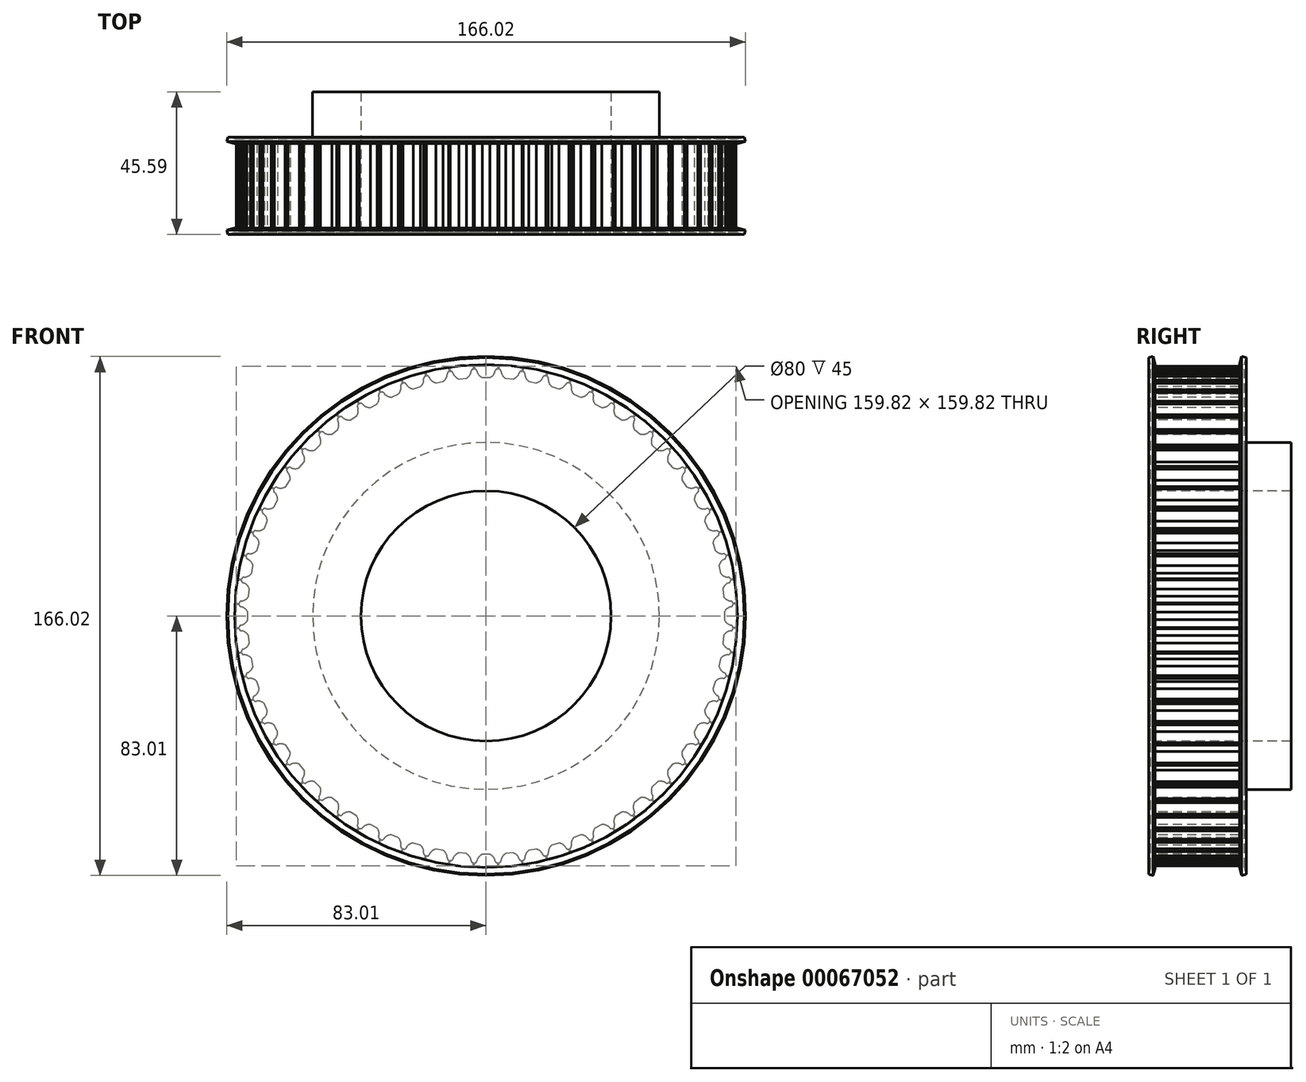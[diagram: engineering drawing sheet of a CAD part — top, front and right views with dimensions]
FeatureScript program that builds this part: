
annotation { "Feature Type Name" : "Feature", "Feature Type Description" : "" }
export const myFeature = defineFeature(function(context is Context, id is Id, definition is map)
    precondition{}
    {
        {
            var Q0;
            Q0=qCreatedBy(makeId("Right.planeOp"),FACE);
            var sketch = newSketch(context, id + "F0", { "sketchPlane" : qUnion([Q0])});
            skLineSegment(sketch, "E0", {"start": v(-21.52, 0) * mm, "end": v(23.89, 0) * mm, "construction": true});
            skLineSegment(sketch, "E1", {"start": v(0, 40) * mm, "end": v(0, 80) * mm});
            skLineSegment(sketch, "E2", {"start": v(0, 80) * mm, "end": v(30, 80) * mm});
            skLineSegment(sketch, "E3", {"start": v(30, 80) * mm, "end": v(30, 55.5) * mm});
            skLineSegment(sketch, "E4", {"start": v(30, 55.5) * mm, "end": v(45, 55.5) * mm});
            skLineSegment(sketch, "E5", {"start": v(45, 55.5) * mm, "end": v(45, 40) * mm});
            skLineSegment(sketch, "E6", {"start": v(45, 40) * mm, "end": v(0, 40) * mm});
            skSolve(sketch);
        }
        {
            var Q0;
            Q0=qSketchRegion(id+"F0",true);
            var Q1;
            Q1=sQuery(id+"F0.wireOp",EDGE,"E0");
            revolve(context, id + "F1", {"entities" : qUnion([Q0]), "axis" : qUnion([Q1]), "revolveType" : RevolveType.FULL});
        }
        {
            var Q0;
            Q0=qCreatedBy(makeId("Right.planeOp"),FACE);
            var sketch = newSketch(context, id + "F2", { "sketchPlane" : qUnion([Q0])});
            skLineSegment(sketch, "E7", {"start": v(-38.96, 0) * mm, "end": v(60.95, 0) * mm, "construction": true});
            skSolve(sketch);
        }
        {
            var Q0;
            Q0=makeQuery(id+"F1.opRevolve","SWEPT_FACE",FACE,{"disambiguationData":[OSD([sQuery(id+"F0.wireOp",EDGE,"E1")])]});
            var sketch = newSketch(context, id + "F3", { "sketchPlane" : qUnion([Q0])});
            skLineSegment(sketch, "E8.bottom", {"start": v(-3.75, 81) * mm, "end": v(3.75, 81) * mm});
            skLineSegment(sketch, "E8.top", {"start": v(3.67, 79) * mm, "end": v(3.75, 79) * mm});
            skLineSegment(sketch, "E8.left", {"start": v(-3.75, 81) * mm, "end": v(-3.75, 79) * mm});
            skLineSegment(sketch, "E8.right", {"start": v(3.75, 81) * mm, "end": v(3.75, 79) * mm});
            skArc(sketch, "E9", {"start": v(-2.94, 78.4) * mm, "mid": v(-2.33, 77.11) * mm, "end": v(-1.2, 76.25) * mm});
            skLineSegment(sketch, "E10", {"start": v(-1.2, 76.25) * mm, "end": v(1.2, 76.25) * mm});
            skArc(sketch, "E11.trimOffspring", {"start": v(1.2, 76.25) * mm, "mid": v(2.33, 77.11) * mm, "end": v(2.94, 78.4) * mm});
            skArc(sketch, "E12.filletArc", {"start": v(3.67, 79) * mm, "mid": v(3.2, 78.83) * mm, "end": v(2.94, 78.4) * mm});
            skLineSegment(sketch, "E13", {"start": v(-3.75, 79) * mm, "end": v(-3.67, 79) * mm});
            skPoint(sketch, "E14.visualSharp", {"position": v(-3, 79) * mm});
            skArc(sketch, "E14.filletArc", {"start": v(-2.94, 78.4) * mm, "mid": v(-3.2, 78.83) * mm, "end": v(-3.67, 79) * mm});
            skLineSegment(sketch, "E15.1.0", {"start": v(-11.67, 80.24) * mm, "end": v(-4.2, 80.98) * mm});
            skLineSegment(sketch, "E15.1.1", {"start": v(-11.67, 80.24) * mm, "end": v(-11.48, 78.25) * mm});
            skLineSegment(sketch, "E15.1.2", {"start": v(-11.48, 78.25) * mm, "end": v(-11.4, 78.26) * mm});
            skArc(sketch, "E15.1.3", {"start": v(-10.6, 77.73) * mm, "mid": v(-10.91, 78.14) * mm, "end": v(-11.4, 78.26) * mm});
            skArc(sketch, "E15.1.4", {"start": v(-10.6, 77.73) * mm, "mid": v(-9.88, 76.51) * mm, "end": v(-8.67, 75.77) * mm});
            skLineSegment(sketch, "E15.1.5", {"start": v(-8.67, 75.77) * mm, "end": v(-6.28, 76) * mm});
            skArc(sketch, "E15.1.6", {"start": v(-6.28, 76) * mm, "mid": v(-5.24, 76.97) * mm, "end": v(-4.76, 78.31) * mm});
            skArc(sketch, "E15.1.7", {"start": v(-4.09, 78.98) * mm, "mid": v(-4.54, 78.76) * mm, "end": v(-4.76, 78.31) * mm});
            skLineSegment(sketch, "E15.1.8", {"start": v(-4.09, 78.98) * mm, "end": v(-4.01, 78.99) * mm});
            skLineSegment(sketch, "E15.1.9", {"start": v(-4.2, 80.98) * mm, "end": v(-4.01, 78.99) * mm});
            skLineSegment(sketch, "E15.2.0", {"start": v(-19.48, 78.71) * mm, "end": v(-12.12, 80.18) * mm});
            skLineSegment(sketch, "E15.2.1", {"start": v(-19.48, 78.71) * mm, "end": v(-19.1, 76.75) * mm});
            skLineSegment(sketch, "E15.2.2", {"start": v(-19.1, 76.75) * mm, "end": v(-19.02, 76.77) * mm});
            skArc(sketch, "E15.2.3", {"start": v(-18.18, 76.32) * mm, "mid": v(-18.52, 76.7) * mm, "end": v(-19.02, 76.77) * mm});
            skArc(sketch, "E15.2.4", {"start": v(-18.18, 76.32) * mm, "mid": v(-17.33, 75.18) * mm, "end": v(-16.05, 74.55) * mm});
            skLineSegment(sketch, "E15.2.5", {"start": v(-16.05, 74.55) * mm, "end": v(-13.7, 75.02) * mm});
            skArc(sketch, "E15.2.6", {"start": v(-13.7, 75.02) * mm, "mid": v(-12.76, 76.09) * mm, "end": v(-12.41, 77.47) * mm});
            skArc(sketch, "E15.2.7", {"start": v(-11.8, 78.2) * mm, "mid": v(-12.24, 77.94) * mm, "end": v(-12.41, 77.47) * mm});
            skLineSegment(sketch, "E15.2.8", {"start": v(-11.8, 78.2) * mm, "end": v(-11.73, 78.21) * mm});
            skLineSegment(sketch, "E15.2.9", {"start": v(-12.12, 80.18) * mm, "end": v(-11.73, 78.21) * mm});
            skLineSegment(sketch, "E15.3.0", {"start": v(-27.1, 76.42) * mm, "end": v(-19.92, 78.6) * mm});
            skLineSegment(sketch, "E15.3.1", {"start": v(-27.1, 76.42) * mm, "end": v(-26.52, 74.5) * mm});
            skLineSegment(sketch, "E15.3.2", {"start": v(-26.52, 74.5) * mm, "end": v(-26.45, 74.53) * mm});
            skArc(sketch, "E15.3.3", {"start": v(-25.57, 74.17) * mm, "mid": v(-25.95, 74.5) * mm, "end": v(-26.45, 74.53) * mm});
            skArc(sketch, "E15.3.4", {"start": v(-25.57, 74.17) * mm, "mid": v(-24.62, 73.12) * mm, "end": v(-23.28, 72.62) * mm});
            skLineSegment(sketch, "E15.3.5", {"start": v(-23.28, 72.62) * mm, "end": v(-20.99, 73.31) * mm});
            skArc(sketch, "E15.3.6", {"start": v(-20.99, 73.31) * mm, "mid": v(-20.15, 74.47) * mm, "end": v(-19.95, 75.88) * mm});
            skArc(sketch, "E15.3.7", {"start": v(-19.42, 76.66) * mm, "mid": v(-19.82, 76.37) * mm, "end": v(-19.95, 75.88) * mm});
            skLineSegment(sketch, "E15.3.8", {"start": v(-19.42, 76.66) * mm, "end": v(-19.34, 76.69) * mm});
            skLineSegment(sketch, "E15.3.9", {"start": v(-19.92, 78.6) * mm, "end": v(-19.34, 76.69) * mm});
            skLineSegment(sketch, "E15.4.0", {"start": v(-34.46, 73.4) * mm, "end": v(-27.53, 76.27) * mm});
            skLineSegment(sketch, "E15.4.1", {"start": v(-34.46, 73.4) * mm, "end": v(-33.7, 71.55) * mm});
            skLineSegment(sketch, "E15.4.2", {"start": v(-33.7, 71.55) * mm, "end": v(-33.63, 71.58) * mm});
            skArc(sketch, "E15.4.3", {"start": v(-32.72, 71.3) * mm, "mid": v(-33.12, 71.6) * mm, "end": v(-33.63, 71.58) * mm});
            skArc(sketch, "E15.4.4", {"start": v(-32.72, 71.3) * mm, "mid": v(-31.66, 70.35) * mm, "end": v(-30.29, 69.99) * mm});
            skLineSegment(sketch, "E15.4.5", {"start": v(-30.29, 69.99) * mm, "end": v(-28.07, 70.9) * mm});
            skArc(sketch, "E15.4.6", {"start": v(-28.07, 70.9) * mm, "mid": v(-27.36, 72.13) * mm, "end": v(-27.29, 73.56) * mm});
            skArc(sketch, "E15.4.7", {"start": v(-26.84, 74.4) * mm, "mid": v(-27.21, 74.05) * mm, "end": v(-27.29, 73.56) * mm});
            skLineSegment(sketch, "E15.4.8", {"start": v(-26.84, 74.4) * mm, "end": v(-26.77, 74.42) * mm});
            skLineSegment(sketch, "E15.4.9", {"start": v(-27.53, 76.27) * mm, "end": v(-26.77, 74.42) * mm});
            skLineSegment(sketch, "E15.5.0", {"start": v(-41.5, 69.67) * mm, "end": v(-34.88, 73.2) * mm});
            skLineSegment(sketch, "E15.5.1", {"start": v(-41.5, 69.67) * mm, "end": v(-40.55, 67.9) * mm});
            skLineSegment(sketch, "E15.5.2", {"start": v(-40.55, 67.9) * mm, "end": v(-40.48, 67.94) * mm});
            skArc(sketch, "E15.5.3", {"start": v(-39.55, 67.76) * mm, "mid": v(-39.98, 68.01) * mm, "end": v(-40.48, 67.94) * mm});
            skArc(sketch, "E15.5.4", {"start": v(-39.55, 67.76) * mm, "mid": v(-38.4, 66.9) * mm, "end": v(-37, 66.68) * mm});
            skLineSegment(sketch, "E15.5.5", {"start": v(-37, 66.68) * mm, "end": v(-34.89, 67.81) * mm});
            skArc(sketch, "E15.5.6", {"start": v(-34.89, 67.81) * mm, "mid": v(-34.3, 69.1) * mm, "end": v(-34.37, 70.53) * mm});
            skArc(sketch, "E15.5.7", {"start": v(-34, 71.4) * mm, "mid": v(-34.34, 71.03) * mm, "end": v(-34.37, 70.53) * mm});
            skLineSegment(sketch, "E15.5.8", {"start": v(-34, 71.4) * mm, "end": v(-33.93, 71.44) * mm});
            skLineSegment(sketch, "E15.5.9", {"start": v(-34.88, 73.2) * mm, "end": v(-33.93, 71.44) * mm});
            skLineSegment(sketch, "E15.6.0", {"start": v(-48.12, 65.27) * mm, "end": v(-41.88, 69.43) * mm});
            skLineSegment(sketch, "E15.6.1", {"start": v(-48.12, 65.27) * mm, "end": v(-47, 63.6) * mm});
            skLineSegment(sketch, "E15.6.2", {"start": v(-47, 63.6) * mm, "end": v(-46.95, 63.64) * mm});
            skArc(sketch, "E15.6.3", {"start": v(-46, 63.55) * mm, "mid": v(-46.46, 63.77) * mm, "end": v(-46.95, 63.64) * mm});
            skArc(sketch, "E15.6.4", {"start": v(-46, 63.55) * mm, "mid": v(-44.78, 62.82) * mm, "end": v(-43.36, 62.73) * mm});
            skLineSegment(sketch, "E15.6.5", {"start": v(-43.36, 62.73) * mm, "end": v(-41.37, 64.07) * mm});
            skArc(sketch, "E15.6.6", {"start": v(-41.37, 64.07) * mm, "mid": v(-40.9, 65.41) * mm, "end": v(-41.11, 66.82) * mm});
            skArc(sketch, "E15.6.7", {"start": v(-40.84, 67.73) * mm, "mid": v(-41.14, 67.32) * mm, "end": v(-41.11, 66.82) * mm});
            skLineSegment(sketch, "E15.6.8", {"start": v(-40.84, 67.73) * mm, "end": v(-40.77, 67.77) * mm});
            skLineSegment(sketch, "E15.6.9", {"start": v(-41.88, 69.43) * mm, "end": v(-40.77, 67.77) * mm});
            skLineSegment(sketch, "E15.7.0", {"start": v(-54.28, 60.23) * mm, "end": v(-48.49, 65) * mm});
            skLineSegment(sketch, "E15.7.1", {"start": v(-54.28, 60.23) * mm, "end": v(-53.02, 58.69) * mm});
            skLineSegment(sketch, "E15.7.2", {"start": v(-53.02, 58.69) * mm, "end": v(-52.96, 58.74) * mm});
            skArc(sketch, "E15.7.3", {"start": v(-52, 58.74) * mm, "mid": v(-52.48, 58.9) * mm, "end": v(-52.96, 58.74) * mm});
            skArc(sketch, "E15.7.4", {"start": v(-52, 58.74) * mm, "mid": v(-50.72, 58.13) * mm, "end": v(-49.3, 58.18) * mm});
            skLineSegment(sketch, "E15.7.5", {"start": v(-49.3, 58.18) * mm, "end": v(-47.45, 59.7) * mm});
            skArc(sketch, "E15.7.6", {"start": v(-47.45, 59.7) * mm, "mid": v(-47.12, 61.09) * mm, "end": v(-47.46, 62.47) * mm});
            skArc(sketch, "E15.7.7", {"start": v(-47.28, 63.4) * mm, "mid": v(-47.54, 62.97) * mm, "end": v(-47.46, 62.47) * mm});
            skLineSegment(sketch, "E15.7.8", {"start": v(-47.28, 63.4) * mm, "end": v(-47.22, 63.45) * mm});
            skLineSegment(sketch, "E15.7.9", {"start": v(-48.49, 65) * mm, "end": v(-47.22, 63.45) * mm});
            skLineSegment(sketch, "E15.8.0", {"start": v(-59.93, 54.62) * mm, "end": v(-54.62, 59.93) * mm});
            skLineSegment(sketch, "E15.8.1", {"start": v(-59.93, 54.62) * mm, "end": v(-58.51, 53.2) * mm});
            skLineSegment(sketch, "E15.8.2", {"start": v(-58.51, 53.2) * mm, "end": v(-58.46, 53.26) * mm});
            skArc(sketch, "E15.8.3", {"start": v(-57.52, 53.36) * mm, "mid": v(-58, 53.48) * mm, "end": v(-58.46, 53.26) * mm});
            skArc(sketch, "E15.8.4", {"start": v(-57.52, 53.36) * mm, "mid": v(-56.18, 52.88) * mm, "end": v(-54.76, 53.07) * mm});
            skLineSegment(sketch, "E15.8.5", {"start": v(-54.76, 53.07) * mm, "end": v(-53.07, 54.76) * mm});
            skArc(sketch, "E15.8.6", {"start": v(-53.07, 54.76) * mm, "mid": v(-52.88, 56.18) * mm, "end": v(-53.36, 57.52) * mm});
            skArc(sketch, "E15.8.7", {"start": v(-53.26, 58.46) * mm, "mid": v(-53.48, 58) * mm, "end": v(-53.36, 57.52) * mm});
            skLineSegment(sketch, "E15.8.8", {"start": v(-53.26, 58.46) * mm, "end": v(-53.2, 58.51) * mm});
            skLineSegment(sketch, "E15.8.9", {"start": v(-54.62, 59.93) * mm, "end": v(-53.2, 58.51) * mm});
            skLineSegment(sketch, "E15.9.0", {"start": v(-65, 48.49) * mm, "end": v(-60.23, 54.28) * mm});
            skLineSegment(sketch, "E15.9.1", {"start": v(-65, 48.49) * mm, "end": v(-63.45, 47.22) * mm});
            skLineSegment(sketch, "E15.9.2", {"start": v(-63.45, 47.22) * mm, "end": v(-63.4, 47.28) * mm});
            skArc(sketch, "E15.9.3", {"start": v(-62.47, 47.46) * mm, "mid": v(-62.97, 47.54) * mm, "end": v(-63.4, 47.28) * mm});
            skArc(sketch, "E15.9.4", {"start": v(-62.47, 47.46) * mm, "mid": v(-61.09, 47.12) * mm, "end": v(-59.7, 47.45) * mm});
            skLineSegment(sketch, "E15.9.5", {"start": v(-59.7, 47.45) * mm, "end": v(-58.18, 49.3) * mm});
            skArc(sketch, "E15.9.6", {"start": v(-58.18, 49.3) * mm, "mid": v(-58.13, 50.72) * mm, "end": v(-58.74, 52) * mm});
            skArc(sketch, "E15.9.7", {"start": v(-58.74, 52.96) * mm, "mid": v(-58.9, 52.48) * mm, "end": v(-58.74, 52) * mm});
            skLineSegment(sketch, "E15.9.8", {"start": v(-58.74, 52.96) * mm, "end": v(-58.69, 53.02) * mm});
            skLineSegment(sketch, "E15.9.9", {"start": v(-60.23, 54.28) * mm, "end": v(-58.69, 53.02) * mm});
            skLineSegment(sketch, "E15.10.0", {"start": v(-69.43, 41.88) * mm, "end": v(-65.27, 48.12) * mm});
            skLineSegment(sketch, "E15.10.1", {"start": v(-69.43, 41.88) * mm, "end": v(-67.77, 40.77) * mm});
            skLineSegment(sketch, "E15.10.2", {"start": v(-67.77, 40.77) * mm, "end": v(-67.73, 40.84) * mm});
            skArc(sketch, "E15.10.3", {"start": v(-66.82, 41.11) * mm, "mid": v(-67.32, 41.14) * mm, "end": v(-67.73, 40.84) * mm});
            skArc(sketch, "E15.10.4", {"start": v(-66.82, 41.11) * mm, "mid": v(-65.41, 40.9) * mm, "end": v(-64.07, 41.37) * mm});
            skLineSegment(sketch, "E15.10.5", {"start": v(-64.07, 41.37) * mm, "end": v(-62.73, 43.36) * mm});
            skArc(sketch, "E15.10.6", {"start": v(-62.73, 43.36) * mm, "mid": v(-62.82, 44.78) * mm, "end": v(-63.55, 46) * mm});
            skArc(sketch, "E15.10.7", {"start": v(-63.64, 46.95) * mm, "mid": v(-63.77, 46.46) * mm, "end": v(-63.55, 46) * mm});
            skLineSegment(sketch, "E15.10.8", {"start": v(-63.64, 46.95) * mm, "end": v(-63.6, 47) * mm});
            skLineSegment(sketch, "E15.10.9", {"start": v(-65.27, 48.12) * mm, "end": v(-63.6, 47) * mm});
            skLineSegment(sketch, "E15.11.0", {"start": v(-73.2, 34.88) * mm, "end": v(-69.67, 41.5) * mm});
            skLineSegment(sketch, "E15.11.1", {"start": v(-73.2, 34.88) * mm, "end": v(-71.44, 33.93) * mm});
            skLineSegment(sketch, "E15.11.2", {"start": v(-71.44, 33.93) * mm, "end": v(-71.4, 34) * mm});
            skArc(sketch, "E15.11.3", {"start": v(-70.53, 34.37) * mm, "mid": v(-71.03, 34.34) * mm, "end": v(-71.4, 34) * mm});
            skArc(sketch, "E15.11.4", {"start": v(-70.53, 34.37) * mm, "mid": v(-69.1, 34.3) * mm, "end": v(-67.81, 34.89) * mm});
            skLineSegment(sketch, "E15.11.5", {"start": v(-67.81, 34.89) * mm, "end": v(-66.68, 37) * mm});
            skArc(sketch, "E15.11.6", {"start": v(-66.68, 37) * mm, "mid": v(-66.9, 38.4) * mm, "end": v(-67.76, 39.55) * mm});
            skArc(sketch, "E15.11.7", {"start": v(-67.94, 40.48) * mm, "mid": v(-68.01, 39.98) * mm, "end": v(-67.76, 39.55) * mm});
            skLineSegment(sketch, "E15.11.8", {"start": v(-67.94, 40.48) * mm, "end": v(-67.9, 40.55) * mm});
            skLineSegment(sketch, "E15.11.9", {"start": v(-69.67, 41.5) * mm, "end": v(-67.9, 40.55) * mm});
            skLineSegment(sketch, "E15.12.0", {"start": v(-76.27, 27.53) * mm, "end": v(-73.4, 34.46) * mm});
            skLineSegment(sketch, "E15.12.1", {"start": v(-76.27, 27.53) * mm, "end": v(-74.42, 26.77) * mm});
            skLineSegment(sketch, "E15.12.2", {"start": v(-74.42, 26.77) * mm, "end": v(-74.4, 26.84) * mm});
            skArc(sketch, "E15.12.3", {"start": v(-73.56, 27.29) * mm, "mid": v(-74.05, 27.21) * mm, "end": v(-74.4, 26.84) * mm});
            skArc(sketch, "E15.12.4", {"start": v(-73.56, 27.29) * mm, "mid": v(-72.13, 27.36) * mm, "end": v(-70.9, 28.07) * mm});
            skLineSegment(sketch, "E15.12.5", {"start": v(-70.9, 28.07) * mm, "end": v(-69.99, 30.29) * mm});
            skArc(sketch, "E15.12.6", {"start": v(-69.99, 30.29) * mm, "mid": v(-70.35, 31.66) * mm, "end": v(-71.3, 32.72) * mm});
            skArc(sketch, "E15.12.7", {"start": v(-71.58, 33.63) * mm, "mid": v(-71.6, 33.12) * mm, "end": v(-71.3, 32.72) * mm});
            skLineSegment(sketch, "E15.12.8", {"start": v(-71.58, 33.63) * mm, "end": v(-71.55, 33.7) * mm});
            skLineSegment(sketch, "E15.12.9", {"start": v(-73.4, 34.46) * mm, "end": v(-71.55, 33.7) * mm});
            skLineSegment(sketch, "E15.13.0", {"start": v(-78.6, 19.92) * mm, "end": v(-76.42, 27.1) * mm});
            skLineSegment(sketch, "E15.13.1", {"start": v(-78.6, 19.92) * mm, "end": v(-76.69, 19.34) * mm});
            skLineSegment(sketch, "E15.13.2", {"start": v(-76.69, 19.34) * mm, "end": v(-76.66, 19.42) * mm});
            skArc(sketch, "E15.13.3", {"start": v(-75.88, 19.95) * mm, "mid": v(-76.37, 19.82) * mm, "end": v(-76.66, 19.42) * mm});
            skArc(sketch, "E15.13.4", {"start": v(-75.88, 19.95) * mm, "mid": v(-74.47, 20.15) * mm, "end": v(-73.31, 20.99) * mm});
            skLineSegment(sketch, "E15.13.5", {"start": v(-73.31, 20.99) * mm, "end": v(-72.62, 23.28) * mm});
            skArc(sketch, "E15.13.6", {"start": v(-72.62, 23.28) * mm, "mid": v(-73.12, 24.62) * mm, "end": v(-74.17, 25.57) * mm});
            skArc(sketch, "E15.13.7", {"start": v(-74.53, 26.45) * mm, "mid": v(-74.5, 25.95) * mm, "end": v(-74.17, 25.57) * mm});
            skLineSegment(sketch, "E15.13.8", {"start": v(-74.53, 26.45) * mm, "end": v(-74.5, 26.52) * mm});
            skLineSegment(sketch, "E15.13.9", {"start": v(-76.42, 27.1) * mm, "end": v(-74.5, 26.52) * mm});
            skLineSegment(sketch, "E15.14.0", {"start": v(-80.18, 12.12) * mm, "end": v(-78.71, 19.48) * mm});
            skLineSegment(sketch, "E15.14.1", {"start": v(-80.18, 12.12) * mm, "end": v(-78.21, 11.73) * mm});
            skLineSegment(sketch, "E15.14.2", {"start": v(-78.21, 11.73) * mm, "end": v(-78.2, 11.8) * mm});
            skArc(sketch, "E15.14.3", {"start": v(-77.47, 12.41) * mm, "mid": v(-77.94, 12.24) * mm, "end": v(-78.2, 11.8) * mm});
            skArc(sketch, "E15.14.4", {"start": v(-77.47, 12.41) * mm, "mid": v(-76.09, 12.76) * mm, "end": v(-75.02, 13.7) * mm});
            skLineSegment(sketch, "E15.14.5", {"start": v(-75.02, 13.7) * mm, "end": v(-74.55, 16.05) * mm});
            skArc(sketch, "E15.14.6", {"start": v(-74.55, 16.05) * mm, "mid": v(-75.18, 17.33) * mm, "end": v(-76.32, 18.18) * mm});
            skArc(sketch, "E15.14.7", {"start": v(-76.77, 19.02) * mm, "mid": v(-76.7, 18.52) * mm, "end": v(-76.32, 18.18) * mm});
            skLineSegment(sketch, "E15.14.8", {"start": v(-76.77, 19.02) * mm, "end": v(-76.75, 19.1) * mm});
            skLineSegment(sketch, "E15.14.9", {"start": v(-78.71, 19.48) * mm, "end": v(-76.75, 19.1) * mm});
            skLineSegment(sketch, "E15.15.0", {"start": v(-80.98, 4.2) * mm, "end": v(-80.24, 11.67) * mm});
            skLineSegment(sketch, "E15.15.1", {"start": v(-80.98, 4.2) * mm, "end": v(-78.99, 4.01) * mm});
            skLineSegment(sketch, "E15.15.2", {"start": v(-78.99, 4.01) * mm, "end": v(-78.98, 4.09) * mm});
            skArc(sketch, "E15.15.3", {"start": v(-78.31, 4.76) * mm, "mid": v(-78.76, 4.54) * mm, "end": v(-78.98, 4.09) * mm});
            skArc(sketch, "E15.15.4", {"start": v(-78.31, 4.76) * mm, "mid": v(-76.97, 5.24) * mm, "end": v(-76, 6.28) * mm});
            skLineSegment(sketch, "E15.15.5", {"start": v(-76, 6.28) * mm, "end": v(-75.77, 8.67) * mm});
            skArc(sketch, "E15.15.6", {"start": v(-75.77, 8.67) * mm, "mid": v(-76.51, 9.88) * mm, "end": v(-77.73, 10.6) * mm});
            skArc(sketch, "E15.15.7", {"start": v(-78.26, 11.4) * mm, "mid": v(-78.14, 10.91) * mm, "end": v(-77.73, 10.6) * mm});
            skLineSegment(sketch, "E15.15.8", {"start": v(-78.26, 11.4) * mm, "end": v(-78.25, 11.48) * mm});
            skLineSegment(sketch, "E15.15.9", {"start": v(-80.24, 11.67) * mm, "end": v(-78.25, 11.48) * mm});
            skLineSegment(sketch, "E15.16.0", {"start": v(-81, -3.75) * mm, "end": v(-81, 3.75) * mm});
            skLineSegment(sketch, "E15.16.1", {"start": v(-81, -3.75) * mm, "end": v(-79, -3.75) * mm});
            skLineSegment(sketch, "E15.16.2", {"start": v(-79, -3.75) * mm, "end": v(-79, -3.67) * mm});
            skArc(sketch, "E15.16.3", {"start": v(-78.4, -2.94) * mm, "mid": v(-78.83, -3.2) * mm, "end": v(-79, -3.67) * mm});
            skArc(sketch, "E15.16.4", {"start": v(-78.4, -2.94) * mm, "mid": v(-77.11, -2.33) * mm, "end": v(-76.25, -1.2) * mm});
            skLineSegment(sketch, "E15.16.5", {"start": v(-76.25, -1.2) * mm, "end": v(-76.25, 1.2) * mm});
            skArc(sketch, "E15.16.6", {"start": v(-76.25, 1.2) * mm, "mid": v(-77.11, 2.33) * mm, "end": v(-78.4, 2.94) * mm});
            skArc(sketch, "E15.16.7", {"start": v(-79, 3.67) * mm, "mid": v(-78.83, 3.2) * mm, "end": v(-78.4, 2.94) * mm});
            skLineSegment(sketch, "E15.16.8", {"start": v(-79, 3.67) * mm, "end": v(-79, 3.75) * mm});
            skLineSegment(sketch, "E15.16.9", {"start": v(-81, 3.75) * mm, "end": v(-79, 3.75) * mm});
            skLineSegment(sketch, "E15.17.0", {"start": v(-80.24, -11.67) * mm, "end": v(-80.98, -4.2) * mm});
            skLineSegment(sketch, "E15.17.1", {"start": v(-80.24, -11.67) * mm, "end": v(-78.25, -11.48) * mm});
            skLineSegment(sketch, "E15.17.2", {"start": v(-78.25, -11.48) * mm, "end": v(-78.26, -11.4) * mm});
            skArc(sketch, "E15.17.3", {"start": v(-77.73, -10.6) * mm, "mid": v(-78.14, -10.91) * mm, "end": v(-78.26, -11.4) * mm});
            skArc(sketch, "E15.17.4", {"start": v(-77.73, -10.6) * mm, "mid": v(-76.51, -9.88) * mm, "end": v(-75.77, -8.67) * mm});
            skLineSegment(sketch, "E15.17.5", {"start": v(-75.77, -8.67) * mm, "end": v(-76, -6.28) * mm});
            skArc(sketch, "E15.17.6", {"start": v(-76, -6.28) * mm, "mid": v(-76.97, -5.24) * mm, "end": v(-78.31, -4.76) * mm});
            skArc(sketch, "E15.17.7", {"start": v(-78.98, -4.09) * mm, "mid": v(-78.76, -4.54) * mm, "end": v(-78.31, -4.76) * mm});
            skLineSegment(sketch, "E15.17.8", {"start": v(-78.98, -4.09) * mm, "end": v(-78.99, -4.01) * mm});
            skLineSegment(sketch, "E15.17.9", {"start": v(-80.98, -4.2) * mm, "end": v(-78.99, -4.01) * mm});
            skLineSegment(sketch, "E15.18.0", {"start": v(-78.71, -19.48) * mm, "end": v(-80.18, -12.12) * mm});
            skLineSegment(sketch, "E15.18.1", {"start": v(-78.71, -19.48) * mm, "end": v(-76.75, -19.1) * mm});
            skLineSegment(sketch, "E15.18.2", {"start": v(-76.75, -19.1) * mm, "end": v(-76.77, -19.02) * mm});
            skArc(sketch, "E15.18.3", {"start": v(-76.32, -18.18) * mm, "mid": v(-76.7, -18.52) * mm, "end": v(-76.77, -19.02) * mm});
            skArc(sketch, "E15.18.4", {"start": v(-76.32, -18.18) * mm, "mid": v(-75.18, -17.33) * mm, "end": v(-74.55, -16.05) * mm});
            skLineSegment(sketch, "E15.18.5", {"start": v(-74.55, -16.05) * mm, "end": v(-75.02, -13.7) * mm});
            skArc(sketch, "E15.18.6", {"start": v(-75.02, -13.7) * mm, "mid": v(-76.09, -12.76) * mm, "end": v(-77.47, -12.41) * mm});
            skArc(sketch, "E15.18.7", {"start": v(-78.2, -11.8) * mm, "mid": v(-77.94, -12.24) * mm, "end": v(-77.47, -12.41) * mm});
            skLineSegment(sketch, "E15.18.8", {"start": v(-78.2, -11.8) * mm, "end": v(-78.21, -11.73) * mm});
            skLineSegment(sketch, "E15.18.9", {"start": v(-80.18, -12.12) * mm, "end": v(-78.21, -11.73) * mm});
            skLineSegment(sketch, "E15.19.0", {"start": v(-76.42, -27.1) * mm, "end": v(-78.6, -19.92) * mm});
            skLineSegment(sketch, "E15.19.1", {"start": v(-76.42, -27.1) * mm, "end": v(-74.5, -26.52) * mm});
            skLineSegment(sketch, "E15.19.2", {"start": v(-74.5, -26.52) * mm, "end": v(-74.53, -26.45) * mm});
            skArc(sketch, "E15.19.3", {"start": v(-74.17, -25.57) * mm, "mid": v(-74.5, -25.95) * mm, "end": v(-74.53, -26.45) * mm});
            skArc(sketch, "E15.19.4", {"start": v(-74.17, -25.57) * mm, "mid": v(-73.12, -24.62) * mm, "end": v(-72.62, -23.28) * mm});
            skLineSegment(sketch, "E15.19.5", {"start": v(-72.62, -23.28) * mm, "end": v(-73.31, -20.99) * mm});
            skArc(sketch, "E15.19.6", {"start": v(-73.31, -20.99) * mm, "mid": v(-74.47, -20.15) * mm, "end": v(-75.88, -19.95) * mm});
            skArc(sketch, "E15.19.7", {"start": v(-76.66, -19.42) * mm, "mid": v(-76.37, -19.82) * mm, "end": v(-75.88, -19.95) * mm});
            skLineSegment(sketch, "E15.19.8", {"start": v(-76.66, -19.42) * mm, "end": v(-76.69, -19.34) * mm});
            skLineSegment(sketch, "E15.19.9", {"start": v(-78.6, -19.92) * mm, "end": v(-76.69, -19.34) * mm});
            skLineSegment(sketch, "E15.20.0", {"start": v(-73.4, -34.46) * mm, "end": v(-76.27, -27.53) * mm});
            skLineSegment(sketch, "E15.20.1", {"start": v(-73.4, -34.46) * mm, "end": v(-71.55, -33.7) * mm});
            skLineSegment(sketch, "E15.20.2", {"start": v(-71.55, -33.7) * mm, "end": v(-71.58, -33.63) * mm});
            skArc(sketch, "E15.20.3", {"start": v(-71.3, -32.72) * mm, "mid": v(-71.6, -33.12) * mm, "end": v(-71.58, -33.63) * mm});
            skArc(sketch, "E15.20.4", {"start": v(-71.3, -32.72) * mm, "mid": v(-70.35, -31.66) * mm, "end": v(-69.99, -30.29) * mm});
            skLineSegment(sketch, "E15.20.5", {"start": v(-69.99, -30.29) * mm, "end": v(-70.9, -28.07) * mm});
            skArc(sketch, "E15.20.6", {"start": v(-70.9, -28.07) * mm, "mid": v(-72.13, -27.36) * mm, "end": v(-73.56, -27.29) * mm});
            skArc(sketch, "E15.20.7", {"start": v(-74.4, -26.84) * mm, "mid": v(-74.05, -27.21) * mm, "end": v(-73.56, -27.29) * mm});
            skLineSegment(sketch, "E15.20.8", {"start": v(-74.4, -26.84) * mm, "end": v(-74.42, -26.77) * mm});
            skLineSegment(sketch, "E15.20.9", {"start": v(-76.27, -27.53) * mm, "end": v(-74.42, -26.77) * mm});
            skLineSegment(sketch, "E15.21.0", {"start": v(-69.67, -41.5) * mm, "end": v(-73.2, -34.88) * mm});
            skLineSegment(sketch, "E15.21.1", {"start": v(-69.67, -41.5) * mm, "end": v(-67.9, -40.55) * mm});
            skLineSegment(sketch, "E15.21.2", {"start": v(-67.9, -40.55) * mm, "end": v(-67.94, -40.48) * mm});
            skArc(sketch, "E15.21.3", {"start": v(-67.76, -39.55) * mm, "mid": v(-68.01, -39.98) * mm, "end": v(-67.94, -40.48) * mm});
            skArc(sketch, "E15.21.4", {"start": v(-67.76, -39.55) * mm, "mid": v(-66.9, -38.4) * mm, "end": v(-66.68, -37) * mm});
            skLineSegment(sketch, "E15.21.5", {"start": v(-66.68, -37) * mm, "end": v(-67.81, -34.89) * mm});
            skArc(sketch, "E15.21.6", {"start": v(-67.81, -34.89) * mm, "mid": v(-69.1, -34.3) * mm, "end": v(-70.53, -34.37) * mm});
            skArc(sketch, "E15.21.7", {"start": v(-71.4, -34) * mm, "mid": v(-71.03, -34.34) * mm, "end": v(-70.53, -34.37) * mm});
            skLineSegment(sketch, "E15.21.8", {"start": v(-71.4, -34) * mm, "end": v(-71.44, -33.93) * mm});
            skLineSegment(sketch, "E15.21.9", {"start": v(-73.2, -34.88) * mm, "end": v(-71.44, -33.93) * mm});
            skPoint(sketch, "E15.center", {"position": v(0, 0) * mm});
            skLineSegment(sketch, "E16.1.22.0", {"start": v(-65.27, -48.12) * mm, "end": v(-69.43, -41.88) * mm});
            skLineSegment(sketch, "E16.3.22.0", {"start": v(-65.27, -48.12) * mm, "end": v(-63.6, -47) * mm});
            skLineSegment(sketch, "E16.6.22.0", {"start": v(-63.6, -47) * mm, "end": v(-63.64, -46.95) * mm});
            skArc(sketch, "E16.9.22.0", {"start": v(-63.55, -46) * mm, "mid": v(-63.77, -46.46) * mm, "end": v(-63.64, -46.95) * mm});
            skArc(sketch, "E16.13.22.0", {"start": v(-63.55, -46) * mm, "mid": v(-62.82, -44.78) * mm, "end": v(-62.73, -43.36) * mm});
            skLineSegment(sketch, "E16.17.22.0", {"start": v(-62.73, -43.36) * mm, "end": v(-64.07, -41.37) * mm});
            skArc(sketch, "E16.20.22.0", {"start": v(-64.07, -41.37) * mm, "mid": v(-65.41, -40.9) * mm, "end": v(-66.82, -41.11) * mm});
            skArc(sketch, "E16.24.22.0", {"start": v(-67.73, -40.84) * mm, "mid": v(-67.32, -41.14) * mm, "end": v(-66.82, -41.11) * mm});
            skLineSegment(sketch, "E16.28.22.0", {"start": v(-67.73, -40.84) * mm, "end": v(-67.77, -40.77) * mm});
            skLineSegment(sketch, "E16.31.22.0", {"start": v(-69.43, -41.88) * mm, "end": v(-67.77, -40.77) * mm});
            skLineSegment(sketch, "E16.1.23.0", {"start": v(-60.23, -54.28) * mm, "end": v(-65, -48.49) * mm});
            skLineSegment(sketch, "E16.3.23.0", {"start": v(-60.23, -54.28) * mm, "end": v(-58.69, -53.02) * mm});
            skLineSegment(sketch, "E16.6.23.0", {"start": v(-58.69, -53.02) * mm, "end": v(-58.74, -52.96) * mm});
            skArc(sketch, "E16.9.23.0", {"start": v(-58.74, -52) * mm, "mid": v(-58.9, -52.48) * mm, "end": v(-58.74, -52.96) * mm});
            skArc(sketch, "E16.13.23.0", {"start": v(-58.74, -52) * mm, "mid": v(-58.13, -50.72) * mm, "end": v(-58.18, -49.3) * mm});
            skLineSegment(sketch, "E16.17.23.0", {"start": v(-58.18, -49.3) * mm, "end": v(-59.7, -47.45) * mm});
            skArc(sketch, "E16.20.23.0", {"start": v(-59.7, -47.45) * mm, "mid": v(-61.09, -47.12) * mm, "end": v(-62.47, -47.46) * mm});
            skArc(sketch, "E16.24.23.0", {"start": v(-63.4, -47.28) * mm, "mid": v(-62.97, -47.54) * mm, "end": v(-62.47, -47.46) * mm});
            skLineSegment(sketch, "E16.28.23.0", {"start": v(-63.4, -47.28) * mm, "end": v(-63.45, -47.22) * mm});
            skLineSegment(sketch, "E16.31.23.0", {"start": v(-65, -48.49) * mm, "end": v(-63.45, -47.22) * mm});
            skLineSegment(sketch, "E16.1.24.0", {"start": v(-54.62, -59.93) * mm, "end": v(-59.93, -54.62) * mm});
            skLineSegment(sketch, "E16.3.24.0", {"start": v(-54.62, -59.93) * mm, "end": v(-53.2, -58.51) * mm});
            skLineSegment(sketch, "E16.6.24.0", {"start": v(-53.2, -58.51) * mm, "end": v(-53.26, -58.46) * mm});
            skArc(sketch, "E16.9.24.0", {"start": v(-53.36, -57.52) * mm, "mid": v(-53.48, -58) * mm, "end": v(-53.26, -58.46) * mm});
            skArc(sketch, "E16.13.24.0", {"start": v(-53.36, -57.52) * mm, "mid": v(-52.88, -56.18) * mm, "end": v(-53.07, -54.76) * mm});
            skLineSegment(sketch, "E16.17.24.0", {"start": v(-53.07, -54.76) * mm, "end": v(-54.76, -53.07) * mm});
            skArc(sketch, "E16.20.24.0", {"start": v(-54.76, -53.07) * mm, "mid": v(-56.18, -52.88) * mm, "end": v(-57.52, -53.36) * mm});
            skArc(sketch, "E16.24.24.0", {"start": v(-58.46, -53.26) * mm, "mid": v(-58, -53.48) * mm, "end": v(-57.52, -53.36) * mm});
            skLineSegment(sketch, "E16.28.24.0", {"start": v(-58.46, -53.26) * mm, "end": v(-58.51, -53.2) * mm});
            skLineSegment(sketch, "E16.31.24.0", {"start": v(-59.93, -54.62) * mm, "end": v(-58.51, -53.2) * mm});
            skLineSegment(sketch, "E16.1.25.0", {"start": v(-48.49, -65) * mm, "end": v(-54.28, -60.23) * mm});
            skLineSegment(sketch, "E16.3.25.0", {"start": v(-48.49, -65) * mm, "end": v(-47.22, -63.45) * mm});
            skLineSegment(sketch, "E16.6.25.0", {"start": v(-47.22, -63.45) * mm, "end": v(-47.28, -63.4) * mm});
            skArc(sketch, "E16.9.25.0", {"start": v(-47.46, -62.47) * mm, "mid": v(-47.54, -62.97) * mm, "end": v(-47.28, -63.4) * mm});
            skArc(sketch, "E16.13.25.0", {"start": v(-47.46, -62.47) * mm, "mid": v(-47.12, -61.09) * mm, "end": v(-47.45, -59.7) * mm});
            skLineSegment(sketch, "E16.17.25.0", {"start": v(-47.45, -59.7) * mm, "end": v(-49.3, -58.18) * mm});
            skArc(sketch, "E16.20.25.0", {"start": v(-49.3, -58.18) * mm, "mid": v(-50.72, -58.13) * mm, "end": v(-52, -58.74) * mm});
            skArc(sketch, "E16.24.25.0", {"start": v(-52.96, -58.74) * mm, "mid": v(-52.48, -58.9) * mm, "end": v(-52, -58.74) * mm});
            skLineSegment(sketch, "E16.28.25.0", {"start": v(-52.96, -58.74) * mm, "end": v(-53.02, -58.69) * mm});
            skLineSegment(sketch, "E16.31.25.0", {"start": v(-54.28, -60.23) * mm, "end": v(-53.02, -58.69) * mm});
            skLineSegment(sketch, "E16.1.26.0", {"start": v(-41.88, -69.43) * mm, "end": v(-48.12, -65.27) * mm});
            skLineSegment(sketch, "E16.3.26.0", {"start": v(-41.88, -69.43) * mm, "end": v(-40.77, -67.77) * mm});
            skLineSegment(sketch, "E16.6.26.0", {"start": v(-40.77, -67.77) * mm, "end": v(-40.84, -67.73) * mm});
            skArc(sketch, "E16.9.26.0", {"start": v(-41.11, -66.82) * mm, "mid": v(-41.14, -67.32) * mm, "end": v(-40.84, -67.73) * mm});
            skArc(sketch, "E16.13.26.0", {"start": v(-41.11, -66.82) * mm, "mid": v(-40.9, -65.41) * mm, "end": v(-41.37, -64.07) * mm});
            skLineSegment(sketch, "E16.17.26.0", {"start": v(-41.37, -64.07) * mm, "end": v(-43.36, -62.73) * mm});
            skArc(sketch, "E16.20.26.0", {"start": v(-43.36, -62.73) * mm, "mid": v(-44.78, -62.82) * mm, "end": v(-46, -63.55) * mm});
            skArc(sketch, "E16.24.26.0", {"start": v(-46.95, -63.64) * mm, "mid": v(-46.46, -63.77) * mm, "end": v(-46, -63.55) * mm});
            skLineSegment(sketch, "E16.28.26.0", {"start": v(-46.95, -63.64) * mm, "end": v(-47, -63.6) * mm});
            skLineSegment(sketch, "E16.31.26.0", {"start": v(-48.12, -65.27) * mm, "end": v(-47, -63.6) * mm});
            skLineSegment(sketch, "E16.1.27.0", {"start": v(-34.88, -73.2) * mm, "end": v(-41.5, -69.67) * mm});
            skLineSegment(sketch, "E16.3.27.0", {"start": v(-34.88, -73.2) * mm, "end": v(-33.93, -71.44) * mm});
            skLineSegment(sketch, "E16.6.27.0", {"start": v(-33.93, -71.44) * mm, "end": v(-34, -71.4) * mm});
            skArc(sketch, "E16.9.27.0", {"start": v(-34.37, -70.53) * mm, "mid": v(-34.34, -71.03) * mm, "end": v(-34, -71.4) * mm});
            skArc(sketch, "E16.13.27.0", {"start": v(-34.37, -70.53) * mm, "mid": v(-34.3, -69.1) * mm, "end": v(-34.89, -67.81) * mm});
            skLineSegment(sketch, "E16.17.27.0", {"start": v(-34.89, -67.81) * mm, "end": v(-37, -66.68) * mm});
            skArc(sketch, "E16.20.27.0", {"start": v(-37, -66.68) * mm, "mid": v(-38.4, -66.9) * mm, "end": v(-39.55, -67.76) * mm});
            skArc(sketch, "E16.24.27.0", {"start": v(-40.48, -67.94) * mm, "mid": v(-39.98, -68.01) * mm, "end": v(-39.55, -67.76) * mm});
            skLineSegment(sketch, "E16.28.27.0", {"start": v(-40.48, -67.94) * mm, "end": v(-40.55, -67.9) * mm});
            skLineSegment(sketch, "E16.31.27.0", {"start": v(-41.5, -69.67) * mm, "end": v(-40.55, -67.9) * mm});
            skLineSegment(sketch, "E16.1.28.0", {"start": v(-27.53, -76.27) * mm, "end": v(-34.46, -73.4) * mm});
            skLineSegment(sketch, "E16.3.28.0", {"start": v(-27.53, -76.27) * mm, "end": v(-26.77, -74.42) * mm});
            skLineSegment(sketch, "E16.6.28.0", {"start": v(-26.77, -74.42) * mm, "end": v(-26.84, -74.4) * mm});
            skArc(sketch, "E16.9.28.0", {"start": v(-27.29, -73.56) * mm, "mid": v(-27.21, -74.05) * mm, "end": v(-26.84, -74.4) * mm});
            skArc(sketch, "E16.13.28.0", {"start": v(-27.29, -73.56) * mm, "mid": v(-27.36, -72.13) * mm, "end": v(-28.07, -70.9) * mm});
            skLineSegment(sketch, "E16.17.28.0", {"start": v(-28.07, -70.9) * mm, "end": v(-30.29, -69.99) * mm});
            skArc(sketch, "E16.20.28.0", {"start": v(-30.29, -69.99) * mm, "mid": v(-31.66, -70.35) * mm, "end": v(-32.72, -71.3) * mm});
            skArc(sketch, "E16.24.28.0", {"start": v(-33.63, -71.58) * mm, "mid": v(-33.12, -71.6) * mm, "end": v(-32.72, -71.3) * mm});
            skLineSegment(sketch, "E16.28.28.0", {"start": v(-33.63, -71.58) * mm, "end": v(-33.7, -71.55) * mm});
            skLineSegment(sketch, "E16.31.28.0", {"start": v(-34.46, -73.4) * mm, "end": v(-33.7, -71.55) * mm});
            skLineSegment(sketch, "E16.1.29.0", {"start": v(-19.92, -78.6) * mm, "end": v(-27.1, -76.42) * mm});
            skLineSegment(sketch, "E16.3.29.0", {"start": v(-19.92, -78.6) * mm, "end": v(-19.34, -76.69) * mm});
            skLineSegment(sketch, "E16.6.29.0", {"start": v(-19.34, -76.69) * mm, "end": v(-19.42, -76.66) * mm});
            skArc(sketch, "E16.9.29.0", {"start": v(-19.95, -75.88) * mm, "mid": v(-19.82, -76.37) * mm, "end": v(-19.42, -76.66) * mm});
            skArc(sketch, "E16.13.29.0", {"start": v(-19.95, -75.88) * mm, "mid": v(-20.15, -74.47) * mm, "end": v(-20.99, -73.31) * mm});
            skLineSegment(sketch, "E16.17.29.0", {"start": v(-20.99, -73.31) * mm, "end": v(-23.28, -72.62) * mm});
            skArc(sketch, "E16.20.29.0", {"start": v(-23.28, -72.62) * mm, "mid": v(-24.62, -73.12) * mm, "end": v(-25.57, -74.17) * mm});
            skArc(sketch, "E16.24.29.0", {"start": v(-26.45, -74.53) * mm, "mid": v(-25.95, -74.5) * mm, "end": v(-25.57, -74.17) * mm});
            skLineSegment(sketch, "E16.28.29.0", {"start": v(-26.45, -74.53) * mm, "end": v(-26.52, -74.5) * mm});
            skLineSegment(sketch, "E16.31.29.0", {"start": v(-27.1, -76.42) * mm, "end": v(-26.52, -74.5) * mm});
            skLineSegment(sketch, "E16.1.30.0", {"start": v(-12.12, -80.18) * mm, "end": v(-19.48, -78.71) * mm});
            skLineSegment(sketch, "E16.3.30.0", {"start": v(-12.12, -80.18) * mm, "end": v(-11.73, -78.21) * mm});
            skLineSegment(sketch, "E16.6.30.0", {"start": v(-11.73, -78.21) * mm, "end": v(-11.8, -78.2) * mm});
            skArc(sketch, "E16.9.30.0", {"start": v(-12.41, -77.47) * mm, "mid": v(-12.24, -77.94) * mm, "end": v(-11.8, -78.2) * mm});
            skArc(sketch, "E16.13.30.0", {"start": v(-12.41, -77.47) * mm, "mid": v(-12.76, -76.09) * mm, "end": v(-13.7, -75.02) * mm});
            skLineSegment(sketch, "E16.17.30.0", {"start": v(-13.7, -75.02) * mm, "end": v(-16.05, -74.55) * mm});
            skArc(sketch, "E16.20.30.0", {"start": v(-16.05, -74.55) * mm, "mid": v(-17.33, -75.18) * mm, "end": v(-18.18, -76.32) * mm});
            skArc(sketch, "E16.24.30.0", {"start": v(-19.02, -76.77) * mm, "mid": v(-18.52, -76.7) * mm, "end": v(-18.18, -76.32) * mm});
            skLineSegment(sketch, "E16.28.30.0", {"start": v(-19.02, -76.77) * mm, "end": v(-19.1, -76.75) * mm});
            skLineSegment(sketch, "E16.31.30.0", {"start": v(-19.48, -78.71) * mm, "end": v(-19.1, -76.75) * mm});
            skLineSegment(sketch, "E16.1.31.0", {"start": v(-4.2, -80.98) * mm, "end": v(-11.67, -80.24) * mm});
            skLineSegment(sketch, "E16.3.31.0", {"start": v(-4.2, -80.98) * mm, "end": v(-4.01, -78.99) * mm});
            skLineSegment(sketch, "E16.6.31.0", {"start": v(-4.01, -78.99) * mm, "end": v(-4.09, -78.98) * mm});
            skArc(sketch, "E16.9.31.0", {"start": v(-4.76, -78.31) * mm, "mid": v(-4.54, -78.76) * mm, "end": v(-4.09, -78.98) * mm});
            skArc(sketch, "E16.13.31.0", {"start": v(-4.76, -78.31) * mm, "mid": v(-5.24, -76.97) * mm, "end": v(-6.28, -76) * mm});
            skLineSegment(sketch, "E16.17.31.0", {"start": v(-6.28, -76) * mm, "end": v(-8.67, -75.77) * mm});
            skArc(sketch, "E16.20.31.0", {"start": v(-8.67, -75.77) * mm, "mid": v(-9.88, -76.51) * mm, "end": v(-10.6, -77.73) * mm});
            skArc(sketch, "E16.24.31.0", {"start": v(-11.4, -78.26) * mm, "mid": v(-10.91, -78.14) * mm, "end": v(-10.6, -77.73) * mm});
            skLineSegment(sketch, "E16.28.31.0", {"start": v(-11.4, -78.26) * mm, "end": v(-11.48, -78.25) * mm});
            skLineSegment(sketch, "E16.31.31.0", {"start": v(-11.67, -80.24) * mm, "end": v(-11.48, -78.25) * mm});
            skLineSegment(sketch, "E16.1.32.0", {"start": v(3.75, -81) * mm, "end": v(-3.75, -81) * mm});
            skLineSegment(sketch, "E16.3.32.0", {"start": v(3.75, -81) * mm, "end": v(3.75, -79) * mm});
            skLineSegment(sketch, "E16.6.32.0", {"start": v(3.75, -79) * mm, "end": v(3.67, -79) * mm});
            skArc(sketch, "E16.9.32.0", {"start": v(2.94, -78.4) * mm, "mid": v(3.2, -78.83) * mm, "end": v(3.67, -79) * mm});
            skArc(sketch, "E16.13.32.0", {"start": v(2.94, -78.4) * mm, "mid": v(2.33, -77.11) * mm, "end": v(1.2, -76.25) * mm});
            skLineSegment(sketch, "E16.17.32.0", {"start": v(1.2, -76.25) * mm, "end": v(-1.2, -76.25) * mm});
            skArc(sketch, "E16.20.32.0", {"start": v(-1.2, -76.25) * mm, "mid": v(-2.33, -77.11) * mm, "end": v(-2.94, -78.4) * mm});
            skArc(sketch, "E16.24.32.0", {"start": v(-3.67, -79) * mm, "mid": v(-3.2, -78.83) * mm, "end": v(-2.94, -78.4) * mm});
            skLineSegment(sketch, "E16.28.32.0", {"start": v(-3.67, -79) * mm, "end": v(-3.75, -79) * mm});
            skLineSegment(sketch, "E16.31.32.0", {"start": v(-3.75, -81) * mm, "end": v(-3.75, -79) * mm});
            skLineSegment(sketch, "E16.1.33.0", {"start": v(11.67, -80.24) * mm, "end": v(4.2, -80.98) * mm});
            skLineSegment(sketch, "E16.3.33.0", {"start": v(11.67, -80.24) * mm, "end": v(11.48, -78.25) * mm});
            skLineSegment(sketch, "E16.6.33.0", {"start": v(11.48, -78.25) * mm, "end": v(11.4, -78.26) * mm});
            skArc(sketch, "E16.9.33.0", {"start": v(10.6, -77.73) * mm, "mid": v(10.91, -78.14) * mm, "end": v(11.4, -78.26) * mm});
            skArc(sketch, "E16.13.33.0", {"start": v(10.6, -77.73) * mm, "mid": v(9.88, -76.51) * mm, "end": v(8.67, -75.77) * mm});
            skLineSegment(sketch, "E16.17.33.0", {"start": v(8.67, -75.77) * mm, "end": v(6.28, -76) * mm});
            skArc(sketch, "E16.20.33.0", {"start": v(6.28, -76) * mm, "mid": v(5.24, -76.97) * mm, "end": v(4.76, -78.31) * mm});
            skArc(sketch, "E16.24.33.0", {"start": v(4.09, -78.98) * mm, "mid": v(4.54, -78.76) * mm, "end": v(4.76, -78.31) * mm});
            skLineSegment(sketch, "E16.28.33.0", {"start": v(4.09, -78.98) * mm, "end": v(4.01, -78.99) * mm});
            skLineSegment(sketch, "E16.31.33.0", {"start": v(4.2, -80.98) * mm, "end": v(4.01, -78.99) * mm});
            skLineSegment(sketch, "E16.1.34.0", {"start": v(19.48, -78.71) * mm, "end": v(12.12, -80.18) * mm});
            skLineSegment(sketch, "E16.3.34.0", {"start": v(19.48, -78.71) * mm, "end": v(19.1, -76.75) * mm});
            skLineSegment(sketch, "E16.6.34.0", {"start": v(19.1, -76.75) * mm, "end": v(19.02, -76.77) * mm});
            skArc(sketch, "E16.9.34.0", {"start": v(18.18, -76.32) * mm, "mid": v(18.52, -76.7) * mm, "end": v(19.02, -76.77) * mm});
            skArc(sketch, "E16.13.34.0", {"start": v(18.18, -76.32) * mm, "mid": v(17.33, -75.18) * mm, "end": v(16.05, -74.55) * mm});
            skLineSegment(sketch, "E16.17.34.0", {"start": v(16.05, -74.55) * mm, "end": v(13.7, -75.02) * mm});
            skArc(sketch, "E16.20.34.0", {"start": v(13.7, -75.02) * mm, "mid": v(12.76, -76.09) * mm, "end": v(12.41, -77.47) * mm});
            skArc(sketch, "E16.24.34.0", {"start": v(11.8, -78.2) * mm, "mid": v(12.24, -77.94) * mm, "end": v(12.41, -77.47) * mm});
            skLineSegment(sketch, "E16.28.34.0", {"start": v(11.8, -78.2) * mm, "end": v(11.73, -78.21) * mm});
            skLineSegment(sketch, "E16.31.34.0", {"start": v(12.12, -80.18) * mm, "end": v(11.73, -78.21) * mm});
            skLineSegment(sketch, "E16.1.35.0", {"start": v(27.1, -76.42) * mm, "end": v(19.92, -78.6) * mm});
            skLineSegment(sketch, "E16.3.35.0", {"start": v(27.1, -76.42) * mm, "end": v(26.52, -74.5) * mm});
            skLineSegment(sketch, "E16.6.35.0", {"start": v(26.52, -74.5) * mm, "end": v(26.45, -74.53) * mm});
            skArc(sketch, "E16.9.35.0", {"start": v(25.57, -74.17) * mm, "mid": v(25.95, -74.5) * mm, "end": v(26.45, -74.53) * mm});
            skArc(sketch, "E16.13.35.0", {"start": v(25.57, -74.17) * mm, "mid": v(24.62, -73.12) * mm, "end": v(23.28, -72.62) * mm});
            skLineSegment(sketch, "E16.17.35.0", {"start": v(23.28, -72.62) * mm, "end": v(20.99, -73.31) * mm});
            skArc(sketch, "E16.20.35.0", {"start": v(20.99, -73.31) * mm, "mid": v(20.15, -74.47) * mm, "end": v(19.95, -75.88) * mm});
            skArc(sketch, "E16.24.35.0", {"start": v(19.42, -76.66) * mm, "mid": v(19.82, -76.37) * mm, "end": v(19.95, -75.88) * mm});
            skLineSegment(sketch, "E16.28.35.0", {"start": v(19.42, -76.66) * mm, "end": v(19.34, -76.69) * mm});
            skLineSegment(sketch, "E16.31.35.0", {"start": v(19.92, -78.6) * mm, "end": v(19.34, -76.69) * mm});
            skLineSegment(sketch, "E16.1.36.0", {"start": v(34.46, -73.4) * mm, "end": v(27.53, -76.27) * mm});
            skLineSegment(sketch, "E16.3.36.0", {"start": v(34.46, -73.4) * mm, "end": v(33.7, -71.55) * mm});
            skLineSegment(sketch, "E16.6.36.0", {"start": v(33.7, -71.55) * mm, "end": v(33.63, -71.58) * mm});
            skArc(sketch, "E16.9.36.0", {"start": v(32.72, -71.3) * mm, "mid": v(33.12, -71.6) * mm, "end": v(33.63, -71.58) * mm});
            skArc(sketch, "E16.13.36.0", {"start": v(32.72, -71.3) * mm, "mid": v(31.66, -70.35) * mm, "end": v(30.29, -69.99) * mm});
            skLineSegment(sketch, "E16.17.36.0", {"start": v(30.29, -69.99) * mm, "end": v(28.07, -70.9) * mm});
            skArc(sketch, "E16.20.36.0", {"start": v(28.07, -70.9) * mm, "mid": v(27.36, -72.13) * mm, "end": v(27.29, -73.56) * mm});
            skArc(sketch, "E16.24.36.0", {"start": v(26.84, -74.4) * mm, "mid": v(27.21, -74.05) * mm, "end": v(27.29, -73.56) * mm});
            skLineSegment(sketch, "E16.28.36.0", {"start": v(26.84, -74.4) * mm, "end": v(26.77, -74.42) * mm});
            skLineSegment(sketch, "E16.31.36.0", {"start": v(27.53, -76.27) * mm, "end": v(26.77, -74.42) * mm});
            skLineSegment(sketch, "E16.1.37.0", {"start": v(41.5, -69.67) * mm, "end": v(34.88, -73.2) * mm});
            skLineSegment(sketch, "E16.3.37.0", {"start": v(41.5, -69.67) * mm, "end": v(40.55, -67.9) * mm});
            skLineSegment(sketch, "E16.6.37.0", {"start": v(40.55, -67.9) * mm, "end": v(40.48, -67.94) * mm});
            skArc(sketch, "E16.9.37.0", {"start": v(39.55, -67.76) * mm, "mid": v(39.98, -68.01) * mm, "end": v(40.48, -67.94) * mm});
            skArc(sketch, "E16.13.37.0", {"start": v(39.55, -67.76) * mm, "mid": v(38.4, -66.9) * mm, "end": v(37, -66.68) * mm});
            skLineSegment(sketch, "E16.17.37.0", {"start": v(37, -66.68) * mm, "end": v(34.89, -67.81) * mm});
            skArc(sketch, "E16.20.37.0", {"start": v(34.89, -67.81) * mm, "mid": v(34.3, -69.1) * mm, "end": v(34.37, -70.53) * mm});
            skArc(sketch, "E16.24.37.0", {"start": v(34, -71.4) * mm, "mid": v(34.34, -71.03) * mm, "end": v(34.37, -70.53) * mm});
            skLineSegment(sketch, "E16.28.37.0", {"start": v(34, -71.4) * mm, "end": v(33.93, -71.44) * mm});
            skLineSegment(sketch, "E16.31.37.0", {"start": v(34.88, -73.2) * mm, "end": v(33.93, -71.44) * mm});
            skLineSegment(sketch, "E16.1.38.0", {"start": v(48.12, -65.27) * mm, "end": v(41.88, -69.43) * mm});
            skLineSegment(sketch, "E16.3.38.0", {"start": v(48.12, -65.27) * mm, "end": v(47, -63.6) * mm});
            skLineSegment(sketch, "E16.6.38.0", {"start": v(47, -63.6) * mm, "end": v(46.95, -63.64) * mm});
            skArc(sketch, "E16.9.38.0", {"start": v(46, -63.55) * mm, "mid": v(46.46, -63.77) * mm, "end": v(46.95, -63.64) * mm});
            skArc(sketch, "E16.13.38.0", {"start": v(46, -63.55) * mm, "mid": v(44.78, -62.82) * mm, "end": v(43.36, -62.73) * mm});
            skLineSegment(sketch, "E16.17.38.0", {"start": v(43.36, -62.73) * mm, "end": v(41.37, -64.07) * mm});
            skArc(sketch, "E16.20.38.0", {"start": v(41.37, -64.07) * mm, "mid": v(40.9, -65.41) * mm, "end": v(41.11, -66.82) * mm});
            skArc(sketch, "E16.24.38.0", {"start": v(40.84, -67.73) * mm, "mid": v(41.14, -67.32) * mm, "end": v(41.11, -66.82) * mm});
            skLineSegment(sketch, "E16.28.38.0", {"start": v(40.84, -67.73) * mm, "end": v(40.77, -67.77) * mm});
            skLineSegment(sketch, "E16.31.38.0", {"start": v(41.88, -69.43) * mm, "end": v(40.77, -67.77) * mm});
            skLineSegment(sketch, "E16.1.39.0", {"start": v(54.28, -60.23) * mm, "end": v(48.49, -65) * mm});
            skLineSegment(sketch, "E16.3.39.0", {"start": v(54.28, -60.23) * mm, "end": v(53.02, -58.69) * mm});
            skLineSegment(sketch, "E16.6.39.0", {"start": v(53.02, -58.69) * mm, "end": v(52.96, -58.74) * mm});
            skArc(sketch, "E16.9.39.0", {"start": v(52, -58.74) * mm, "mid": v(52.48, -58.9) * mm, "end": v(52.96, -58.74) * mm});
            skArc(sketch, "E16.13.39.0", {"start": v(52, -58.74) * mm, "mid": v(50.72, -58.13) * mm, "end": v(49.3, -58.18) * mm});
            skLineSegment(sketch, "E16.17.39.0", {"start": v(49.3, -58.18) * mm, "end": v(47.45, -59.7) * mm});
            skArc(sketch, "E16.20.39.0", {"start": v(47.45, -59.7) * mm, "mid": v(47.12, -61.09) * mm, "end": v(47.46, -62.47) * mm});
            skArc(sketch, "E16.24.39.0", {"start": v(47.28, -63.4) * mm, "mid": v(47.54, -62.97) * mm, "end": v(47.46, -62.47) * mm});
            skLineSegment(sketch, "E16.28.39.0", {"start": v(47.28, -63.4) * mm, "end": v(47.22, -63.45) * mm});
            skLineSegment(sketch, "E16.31.39.0", {"start": v(48.49, -65) * mm, "end": v(47.22, -63.45) * mm});
            skLineSegment(sketch, "E16.1.40.0", {"start": v(59.93, -54.62) * mm, "end": v(54.62, -59.93) * mm});
            skLineSegment(sketch, "E16.3.40.0", {"start": v(59.93, -54.62) * mm, "end": v(58.51, -53.2) * mm});
            skLineSegment(sketch, "E16.6.40.0", {"start": v(58.51, -53.2) * mm, "end": v(58.46, -53.26) * mm});
            skArc(sketch, "E16.9.40.0", {"start": v(57.52, -53.36) * mm, "mid": v(58, -53.48) * mm, "end": v(58.46, -53.26) * mm});
            skArc(sketch, "E16.13.40.0", {"start": v(57.52, -53.36) * mm, "mid": v(56.18, -52.88) * mm, "end": v(54.76, -53.07) * mm});
            skLineSegment(sketch, "E16.17.40.0", {"start": v(54.76, -53.07) * mm, "end": v(53.07, -54.76) * mm});
            skArc(sketch, "E16.20.40.0", {"start": v(53.07, -54.76) * mm, "mid": v(52.88, -56.18) * mm, "end": v(53.36, -57.52) * mm});
            skArc(sketch, "E16.24.40.0", {"start": v(53.26, -58.46) * mm, "mid": v(53.48, -58) * mm, "end": v(53.36, -57.52) * mm});
            skLineSegment(sketch, "E16.28.40.0", {"start": v(53.26, -58.46) * mm, "end": v(53.2, -58.51) * mm});
            skLineSegment(sketch, "E16.31.40.0", {"start": v(54.62, -59.93) * mm, "end": v(53.2, -58.51) * mm});
            skLineSegment(sketch, "E16.1.41.0", {"start": v(65, -48.49) * mm, "end": v(60.23, -54.28) * mm});
            skLineSegment(sketch, "E16.3.41.0", {"start": v(65, -48.49) * mm, "end": v(63.45, -47.22) * mm});
            skLineSegment(sketch, "E16.6.41.0", {"start": v(63.45, -47.22) * mm, "end": v(63.4, -47.28) * mm});
            skArc(sketch, "E16.9.41.0", {"start": v(62.47, -47.46) * mm, "mid": v(62.97, -47.54) * mm, "end": v(63.4, -47.28) * mm});
            skArc(sketch, "E16.13.41.0", {"start": v(62.47, -47.46) * mm, "mid": v(61.09, -47.12) * mm, "end": v(59.7, -47.45) * mm});
            skLineSegment(sketch, "E16.17.41.0", {"start": v(59.7, -47.45) * mm, "end": v(58.18, -49.3) * mm});
            skArc(sketch, "E16.20.41.0", {"start": v(58.18, -49.3) * mm, "mid": v(58.13, -50.72) * mm, "end": v(58.74, -52) * mm});
            skArc(sketch, "E16.24.41.0", {"start": v(58.74, -52.96) * mm, "mid": v(58.9, -52.48) * mm, "end": v(58.74, -52) * mm});
            skLineSegment(sketch, "E16.28.41.0", {"start": v(58.74, -52.96) * mm, "end": v(58.69, -53.02) * mm});
            skLineSegment(sketch, "E16.31.41.0", {"start": v(60.23, -54.28) * mm, "end": v(58.69, -53.02) * mm});
            skLineSegment(sketch, "E16.1.42.0", {"start": v(69.43, -41.88) * mm, "end": v(65.27, -48.12) * mm});
            skLineSegment(sketch, "E16.3.42.0", {"start": v(69.43, -41.88) * mm, "end": v(67.77, -40.77) * mm});
            skLineSegment(sketch, "E16.6.42.0", {"start": v(67.77, -40.77) * mm, "end": v(67.73, -40.84) * mm});
            skArc(sketch, "E16.9.42.0", {"start": v(66.82, -41.11) * mm, "mid": v(67.32, -41.14) * mm, "end": v(67.73, -40.84) * mm});
            skArc(sketch, "E16.13.42.0", {"start": v(66.82, -41.11) * mm, "mid": v(65.41, -40.9) * mm, "end": v(64.07, -41.37) * mm});
            skLineSegment(sketch, "E16.17.42.0", {"start": v(64.07, -41.37) * mm, "end": v(62.73, -43.36) * mm});
            skArc(sketch, "E16.20.42.0", {"start": v(62.73, -43.36) * mm, "mid": v(62.82, -44.78) * mm, "end": v(63.55, -46) * mm});
            skArc(sketch, "E16.24.42.0", {"start": v(63.64, -46.95) * mm, "mid": v(63.77, -46.46) * mm, "end": v(63.55, -46) * mm});
            skLineSegment(sketch, "E16.28.42.0", {"start": v(63.64, -46.95) * mm, "end": v(63.6, -47) * mm});
            skLineSegment(sketch, "E16.31.42.0", {"start": v(65.27, -48.12) * mm, "end": v(63.6, -47) * mm});
            skLineSegment(sketch, "E16.1.43.0", {"start": v(73.2, -34.88) * mm, "end": v(69.67, -41.5) * mm});
            skLineSegment(sketch, "E16.3.43.0", {"start": v(73.2, -34.88) * mm, "end": v(71.44, -33.93) * mm});
            skLineSegment(sketch, "E16.6.43.0", {"start": v(71.44, -33.93) * mm, "end": v(71.4, -34) * mm});
            skArc(sketch, "E16.9.43.0", {"start": v(70.53, -34.37) * mm, "mid": v(71.03, -34.34) * mm, "end": v(71.4, -34) * mm});
            skArc(sketch, "E16.13.43.0", {"start": v(70.53, -34.37) * mm, "mid": v(69.1, -34.3) * mm, "end": v(67.81, -34.89) * mm});
            skLineSegment(sketch, "E16.17.43.0", {"start": v(67.81, -34.89) * mm, "end": v(66.68, -37) * mm});
            skArc(sketch, "E16.20.43.0", {"start": v(66.68, -37) * mm, "mid": v(66.9, -38.4) * mm, "end": v(67.76, -39.55) * mm});
            skArc(sketch, "E16.24.43.0", {"start": v(67.94, -40.48) * mm, "mid": v(68.01, -39.98) * mm, "end": v(67.76, -39.55) * mm});
            skLineSegment(sketch, "E16.28.43.0", {"start": v(67.94, -40.48) * mm, "end": v(67.9, -40.55) * mm});
            skLineSegment(sketch, "E16.31.43.0", {"start": v(69.67, -41.5) * mm, "end": v(67.9, -40.55) * mm});
            skLineSegment(sketch, "E16.1.44.0", {"start": v(76.27, -27.53) * mm, "end": v(73.4, -34.46) * mm});
            skLineSegment(sketch, "E16.3.44.0", {"start": v(76.27, -27.53) * mm, "end": v(74.42, -26.77) * mm});
            skLineSegment(sketch, "E16.6.44.0", {"start": v(74.42, -26.77) * mm, "end": v(74.4, -26.84) * mm});
            skArc(sketch, "E16.9.44.0", {"start": v(73.56, -27.29) * mm, "mid": v(74.05, -27.21) * mm, "end": v(74.4, -26.84) * mm});
            skArc(sketch, "E16.13.44.0", {"start": v(73.56, -27.29) * mm, "mid": v(72.13, -27.36) * mm, "end": v(70.9, -28.07) * mm});
            skLineSegment(sketch, "E16.17.44.0", {"start": v(70.9, -28.07) * mm, "end": v(69.99, -30.29) * mm});
            skArc(sketch, "E16.20.44.0", {"start": v(69.99, -30.29) * mm, "mid": v(70.35, -31.66) * mm, "end": v(71.3, -32.72) * mm});
            skArc(sketch, "E16.24.44.0", {"start": v(71.58, -33.63) * mm, "mid": v(71.6, -33.12) * mm, "end": v(71.3, -32.72) * mm});
            skLineSegment(sketch, "E16.28.44.0", {"start": v(71.58, -33.63) * mm, "end": v(71.55, -33.7) * mm});
            skLineSegment(sketch, "E16.31.44.0", {"start": v(73.4, -34.46) * mm, "end": v(71.55, -33.7) * mm});
            skLineSegment(sketch, "E16.1.45.0", {"start": v(78.6, -19.92) * mm, "end": v(76.42, -27.1) * mm});
            skLineSegment(sketch, "E16.3.45.0", {"start": v(78.6, -19.92) * mm, "end": v(76.69, -19.34) * mm});
            skLineSegment(sketch, "E16.6.45.0", {"start": v(76.69, -19.34) * mm, "end": v(76.66, -19.42) * mm});
            skArc(sketch, "E16.9.45.0", {"start": v(75.88, -19.95) * mm, "mid": v(76.37, -19.82) * mm, "end": v(76.66, -19.42) * mm});
            skArc(sketch, "E16.13.45.0", {"start": v(75.88, -19.95) * mm, "mid": v(74.47, -20.15) * mm, "end": v(73.31, -20.99) * mm});
            skLineSegment(sketch, "E16.17.45.0", {"start": v(73.31, -20.99) * mm, "end": v(72.62, -23.28) * mm});
            skArc(sketch, "E16.20.45.0", {"start": v(72.62, -23.28) * mm, "mid": v(73.12, -24.62) * mm, "end": v(74.17, -25.57) * mm});
            skArc(sketch, "E16.24.45.0", {"start": v(74.53, -26.45) * mm, "mid": v(74.5, -25.95) * mm, "end": v(74.17, -25.57) * mm});
            skLineSegment(sketch, "E16.28.45.0", {"start": v(74.53, -26.45) * mm, "end": v(74.5, -26.52) * mm});
            skLineSegment(sketch, "E16.31.45.0", {"start": v(76.42, -27.1) * mm, "end": v(74.5, -26.52) * mm});
            skLineSegment(sketch, "E16.1.46.0", {"start": v(80.18, -12.12) * mm, "end": v(78.71, -19.48) * mm});
            skLineSegment(sketch, "E16.3.46.0", {"start": v(80.18, -12.12) * mm, "end": v(78.21, -11.73) * mm});
            skLineSegment(sketch, "E16.6.46.0", {"start": v(78.21, -11.73) * mm, "end": v(78.2, -11.8) * mm});
            skArc(sketch, "E16.9.46.0", {"start": v(77.47, -12.41) * mm, "mid": v(77.94, -12.24) * mm, "end": v(78.2, -11.8) * mm});
            skArc(sketch, "E16.13.46.0", {"start": v(77.47, -12.41) * mm, "mid": v(76.09, -12.76) * mm, "end": v(75.02, -13.7) * mm});
            skLineSegment(sketch, "E16.17.46.0", {"start": v(75.02, -13.7) * mm, "end": v(74.55, -16.05) * mm});
            skArc(sketch, "E16.20.46.0", {"start": v(74.55, -16.05) * mm, "mid": v(75.18, -17.33) * mm, "end": v(76.32, -18.18) * mm});
            skArc(sketch, "E16.24.46.0", {"start": v(76.77, -19.02) * mm, "mid": v(76.7, -18.52) * mm, "end": v(76.32, -18.18) * mm});
            skLineSegment(sketch, "E16.28.46.0", {"start": v(76.77, -19.02) * mm, "end": v(76.75, -19.1) * mm});
            skLineSegment(sketch, "E16.31.46.0", {"start": v(78.71, -19.48) * mm, "end": v(76.75, -19.1) * mm});
            skLineSegment(sketch, "E16.1.47.0", {"start": v(80.98, -4.2) * mm, "end": v(80.24, -11.67) * mm});
            skLineSegment(sketch, "E16.3.47.0", {"start": v(80.98, -4.2) * mm, "end": v(78.99, -4.01) * mm});
            skLineSegment(sketch, "E16.6.47.0", {"start": v(78.99, -4.01) * mm, "end": v(78.98, -4.09) * mm});
            skArc(sketch, "E16.9.47.0", {"start": v(78.31, -4.76) * mm, "mid": v(78.76, -4.54) * mm, "end": v(78.98, -4.09) * mm});
            skArc(sketch, "E16.13.47.0", {"start": v(78.31, -4.76) * mm, "mid": v(76.97, -5.24) * mm, "end": v(76, -6.28) * mm});
            skLineSegment(sketch, "E16.17.47.0", {"start": v(76, -6.28) * mm, "end": v(75.77, -8.67) * mm});
            skArc(sketch, "E16.20.47.0", {"start": v(75.77, -8.67) * mm, "mid": v(76.51, -9.88) * mm, "end": v(77.73, -10.6) * mm});
            skArc(sketch, "E16.24.47.0", {"start": v(78.26, -11.4) * mm, "mid": v(78.14, -10.91) * mm, "end": v(77.73, -10.6) * mm});
            skLineSegment(sketch, "E16.28.47.0", {"start": v(78.26, -11.4) * mm, "end": v(78.25, -11.48) * mm});
            skLineSegment(sketch, "E16.31.47.0", {"start": v(80.24, -11.67) * mm, "end": v(78.25, -11.48) * mm});
            skLineSegment(sketch, "E16.1.48.0", {"start": v(81, 3.75) * mm, "end": v(81, -3.75) * mm});
            skLineSegment(sketch, "E16.3.48.0", {"start": v(81, 3.75) * mm, "end": v(79, 3.75) * mm});
            skLineSegment(sketch, "E16.6.48.0", {"start": v(79, 3.75) * mm, "end": v(79, 3.67) * mm});
            skArc(sketch, "E16.9.48.0", {"start": v(78.4, 2.94) * mm, "mid": v(78.83, 3.2) * mm, "end": v(79, 3.67) * mm});
            skArc(sketch, "E16.13.48.0", {"start": v(78.4, 2.94) * mm, "mid": v(77.11, 2.33) * mm, "end": v(76.25, 1.2) * mm});
            skLineSegment(sketch, "E16.17.48.0", {"start": v(76.25, 1.2) * mm, "end": v(76.25, -1.2) * mm});
            skArc(sketch, "E16.20.48.0", {"start": v(76.25, -1.2) * mm, "mid": v(77.11, -2.33) * mm, "end": v(78.4, -2.94) * mm});
            skArc(sketch, "E16.24.48.0", {"start": v(79, -3.67) * mm, "mid": v(78.83, -3.2) * mm, "end": v(78.4, -2.94) * mm});
            skLineSegment(sketch, "E16.28.48.0", {"start": v(79, -3.67) * mm, "end": v(79, -3.75) * mm});
            skLineSegment(sketch, "E16.31.48.0", {"start": v(81, -3.75) * mm, "end": v(79, -3.75) * mm});
            skLineSegment(sketch, "E16.1.49.0", {"start": v(80.24, 11.67) * mm, "end": v(80.98, 4.2) * mm});
            skLineSegment(sketch, "E16.3.49.0", {"start": v(80.24, 11.67) * mm, "end": v(78.25, 11.48) * mm});
            skLineSegment(sketch, "E16.6.49.0", {"start": v(78.25, 11.48) * mm, "end": v(78.26, 11.4) * mm});
            skArc(sketch, "E16.9.49.0", {"start": v(77.73, 10.6) * mm, "mid": v(78.14, 10.91) * mm, "end": v(78.26, 11.4) * mm});
            skArc(sketch, "E16.13.49.0", {"start": v(77.73, 10.6) * mm, "mid": v(76.51, 9.88) * mm, "end": v(75.77, 8.67) * mm});
            skLineSegment(sketch, "E16.17.49.0", {"start": v(75.77, 8.67) * mm, "end": v(76, 6.28) * mm});
            skArc(sketch, "E16.20.49.0", {"start": v(76, 6.28) * mm, "mid": v(76.97, 5.24) * mm, "end": v(78.31, 4.76) * mm});
            skArc(sketch, "E16.24.49.0", {"start": v(78.98, 4.09) * mm, "mid": v(78.76, 4.54) * mm, "end": v(78.31, 4.76) * mm});
            skLineSegment(sketch, "E16.28.49.0", {"start": v(78.98, 4.09) * mm, "end": v(78.99, 4.01) * mm});
            skLineSegment(sketch, "E16.31.49.0", {"start": v(80.98, 4.2) * mm, "end": v(78.99, 4.01) * mm});
            skLineSegment(sketch, "E16.1.50.0", {"start": v(78.71, 19.48) * mm, "end": v(80.18, 12.12) * mm});
            skLineSegment(sketch, "E16.3.50.0", {"start": v(78.71, 19.48) * mm, "end": v(76.75, 19.1) * mm});
            skLineSegment(sketch, "E16.6.50.0", {"start": v(76.75, 19.1) * mm, "end": v(76.77, 19.02) * mm});
            skArc(sketch, "E16.9.50.0", {"start": v(76.32, 18.18) * mm, "mid": v(76.7, 18.52) * mm, "end": v(76.77, 19.02) * mm});
            skArc(sketch, "E16.13.50.0", {"start": v(76.32, 18.18) * mm, "mid": v(75.18, 17.33) * mm, "end": v(74.55, 16.05) * mm});
            skLineSegment(sketch, "E16.17.50.0", {"start": v(74.55, 16.05) * mm, "end": v(75.02, 13.7) * mm});
            skArc(sketch, "E16.20.50.0", {"start": v(75.02, 13.7) * mm, "mid": v(76.09, 12.76) * mm, "end": v(77.47, 12.41) * mm});
            skArc(sketch, "E16.24.50.0", {"start": v(78.2, 11.8) * mm, "mid": v(77.94, 12.24) * mm, "end": v(77.47, 12.41) * mm});
            skLineSegment(sketch, "E16.28.50.0", {"start": v(78.2, 11.8) * mm, "end": v(78.21, 11.73) * mm});
            skLineSegment(sketch, "E16.31.50.0", {"start": v(80.18, 12.12) * mm, "end": v(78.21, 11.73) * mm});
            skLineSegment(sketch, "E16.1.51.0", {"start": v(76.42, 27.1) * mm, "end": v(78.6, 19.92) * mm});
            skLineSegment(sketch, "E16.3.51.0", {"start": v(76.42, 27.1) * mm, "end": v(74.5, 26.52) * mm});
            skLineSegment(sketch, "E16.6.51.0", {"start": v(74.5, 26.52) * mm, "end": v(74.53, 26.45) * mm});
            skArc(sketch, "E16.9.51.0", {"start": v(74.17, 25.57) * mm, "mid": v(74.5, 25.95) * mm, "end": v(74.53, 26.45) * mm});
            skArc(sketch, "E16.13.51.0", {"start": v(74.17, 25.57) * mm, "mid": v(73.12, 24.62) * mm, "end": v(72.62, 23.28) * mm});
            skLineSegment(sketch, "E16.17.51.0", {"start": v(72.62, 23.28) * mm, "end": v(73.31, 20.99) * mm});
            skArc(sketch, "E16.20.51.0", {"start": v(73.31, 20.99) * mm, "mid": v(74.47, 20.15) * mm, "end": v(75.88, 19.95) * mm});
            skArc(sketch, "E16.24.51.0", {"start": v(76.66, 19.42) * mm, "mid": v(76.37, 19.82) * mm, "end": v(75.88, 19.95) * mm});
            skLineSegment(sketch, "E16.28.51.0", {"start": v(76.66, 19.42) * mm, "end": v(76.69, 19.34) * mm});
            skLineSegment(sketch, "E16.31.51.0", {"start": v(78.6, 19.92) * mm, "end": v(76.69, 19.34) * mm});
            skLineSegment(sketch, "E16.1.52.0", {"start": v(73.4, 34.46) * mm, "end": v(76.27, 27.53) * mm});
            skLineSegment(sketch, "E16.3.52.0", {"start": v(73.4, 34.46) * mm, "end": v(71.55, 33.7) * mm});
            skLineSegment(sketch, "E16.6.52.0", {"start": v(71.55, 33.7) * mm, "end": v(71.58, 33.63) * mm});
            skArc(sketch, "E16.9.52.0", {"start": v(71.3, 32.72) * mm, "mid": v(71.6, 33.12) * mm, "end": v(71.58, 33.63) * mm});
            skArc(sketch, "E16.13.52.0", {"start": v(71.3, 32.72) * mm, "mid": v(70.35, 31.66) * mm, "end": v(69.99, 30.29) * mm});
            skLineSegment(sketch, "E16.17.52.0", {"start": v(69.99, 30.29) * mm, "end": v(70.9, 28.07) * mm});
            skArc(sketch, "E16.20.52.0", {"start": v(70.9, 28.07) * mm, "mid": v(72.13, 27.36) * mm, "end": v(73.56, 27.29) * mm});
            skArc(sketch, "E16.24.52.0", {"start": v(74.4, 26.84) * mm, "mid": v(74.05, 27.21) * mm, "end": v(73.56, 27.29) * mm});
            skLineSegment(sketch, "E16.28.52.0", {"start": v(74.4, 26.84) * mm, "end": v(74.42, 26.77) * mm});
            skLineSegment(sketch, "E16.31.52.0", {"start": v(76.27, 27.53) * mm, "end": v(74.42, 26.77) * mm});
            skLineSegment(sketch, "E16.1.53.0", {"start": v(69.67, 41.5) * mm, "end": v(73.2, 34.88) * mm});
            skLineSegment(sketch, "E16.3.53.0", {"start": v(69.67, 41.5) * mm, "end": v(67.9, 40.55) * mm});
            skLineSegment(sketch, "E16.6.53.0", {"start": v(67.9, 40.55) * mm, "end": v(67.94, 40.48) * mm});
            skArc(sketch, "E16.9.53.0", {"start": v(67.76, 39.55) * mm, "mid": v(68.01, 39.98) * mm, "end": v(67.94, 40.48) * mm});
            skArc(sketch, "E16.13.53.0", {"start": v(67.76, 39.55) * mm, "mid": v(66.9, 38.4) * mm, "end": v(66.68, 37) * mm});
            skLineSegment(sketch, "E16.17.53.0", {"start": v(66.68, 37) * mm, "end": v(67.81, 34.89) * mm});
            skArc(sketch, "E16.20.53.0", {"start": v(67.81, 34.89) * mm, "mid": v(69.1, 34.3) * mm, "end": v(70.53, 34.37) * mm});
            skArc(sketch, "E16.24.53.0", {"start": v(71.4, 34) * mm, "mid": v(71.03, 34.34) * mm, "end": v(70.53, 34.37) * mm});
            skLineSegment(sketch, "E16.28.53.0", {"start": v(71.4, 34) * mm, "end": v(71.44, 33.93) * mm});
            skLineSegment(sketch, "E16.31.53.0", {"start": v(73.2, 34.88) * mm, "end": v(71.44, 33.93) * mm});
            skLineSegment(sketch, "E16.1.54.0", {"start": v(65.27, 48.12) * mm, "end": v(69.43, 41.88) * mm});
            skLineSegment(sketch, "E16.3.54.0", {"start": v(65.27, 48.12) * mm, "end": v(63.6, 47) * mm});
            skLineSegment(sketch, "E16.6.54.0", {"start": v(63.6, 47) * mm, "end": v(63.64, 46.95) * mm});
            skArc(sketch, "E16.9.54.0", {"start": v(63.55, 46) * mm, "mid": v(63.77, 46.46) * mm, "end": v(63.64, 46.95) * mm});
            skArc(sketch, "E16.13.54.0", {"start": v(63.55, 46) * mm, "mid": v(62.82, 44.78) * mm, "end": v(62.73, 43.36) * mm});
            skLineSegment(sketch, "E16.17.54.0", {"start": v(62.73, 43.36) * mm, "end": v(64.07, 41.37) * mm});
            skArc(sketch, "E16.20.54.0", {"start": v(64.07, 41.37) * mm, "mid": v(65.41, 40.9) * mm, "end": v(66.82, 41.11) * mm});
            skArc(sketch, "E16.24.54.0", {"start": v(67.73, 40.84) * mm, "mid": v(67.32, 41.14) * mm, "end": v(66.82, 41.11) * mm});
            skLineSegment(sketch, "E16.28.54.0", {"start": v(67.73, 40.84) * mm, "end": v(67.77, 40.77) * mm});
            skLineSegment(sketch, "E16.31.54.0", {"start": v(69.43, 41.88) * mm, "end": v(67.77, 40.77) * mm});
            skLineSegment(sketch, "E16.1.55.0", {"start": v(60.23, 54.28) * mm, "end": v(65, 48.49) * mm});
            skLineSegment(sketch, "E16.3.55.0", {"start": v(60.23, 54.28) * mm, "end": v(58.69, 53.02) * mm});
            skLineSegment(sketch, "E16.6.55.0", {"start": v(58.69, 53.02) * mm, "end": v(58.74, 52.96) * mm});
            skArc(sketch, "E16.9.55.0", {"start": v(58.74, 52) * mm, "mid": v(58.9, 52.48) * mm, "end": v(58.74, 52.96) * mm});
            skArc(sketch, "E16.13.55.0", {"start": v(58.74, 52) * mm, "mid": v(58.13, 50.72) * mm, "end": v(58.18, 49.3) * mm});
            skLineSegment(sketch, "E16.17.55.0", {"start": v(58.18, 49.3) * mm, "end": v(59.7, 47.45) * mm});
            skArc(sketch, "E16.20.55.0", {"start": v(59.7, 47.45) * mm, "mid": v(61.09, 47.12) * mm, "end": v(62.47, 47.46) * mm});
            skArc(sketch, "E16.24.55.0", {"start": v(63.4, 47.28) * mm, "mid": v(62.97, 47.54) * mm, "end": v(62.47, 47.46) * mm});
            skLineSegment(sketch, "E16.28.55.0", {"start": v(63.4, 47.28) * mm, "end": v(63.45, 47.22) * mm});
            skLineSegment(sketch, "E16.31.55.0", {"start": v(65, 48.49) * mm, "end": v(63.45, 47.22) * mm});
            skLineSegment(sketch, "E16.1.56.0", {"start": v(54.62, 59.93) * mm, "end": v(59.93, 54.62) * mm});
            skLineSegment(sketch, "E16.3.56.0", {"start": v(54.62, 59.93) * mm, "end": v(53.2, 58.51) * mm});
            skLineSegment(sketch, "E16.6.56.0", {"start": v(53.2, 58.51) * mm, "end": v(53.26, 58.46) * mm});
            skArc(sketch, "E16.9.56.0", {"start": v(53.36, 57.52) * mm, "mid": v(53.48, 58) * mm, "end": v(53.26, 58.46) * mm});
            skArc(sketch, "E16.13.56.0", {"start": v(53.36, 57.52) * mm, "mid": v(52.88, 56.18) * mm, "end": v(53.07, 54.76) * mm});
            skLineSegment(sketch, "E16.17.56.0", {"start": v(53.07, 54.76) * mm, "end": v(54.76, 53.07) * mm});
            skArc(sketch, "E16.20.56.0", {"start": v(54.76, 53.07) * mm, "mid": v(56.18, 52.88) * mm, "end": v(57.52, 53.36) * mm});
            skArc(sketch, "E16.24.56.0", {"start": v(58.46, 53.26) * mm, "mid": v(58, 53.48) * mm, "end": v(57.52, 53.36) * mm});
            skLineSegment(sketch, "E16.28.56.0", {"start": v(58.46, 53.26) * mm, "end": v(58.51, 53.2) * mm});
            skLineSegment(sketch, "E16.31.56.0", {"start": v(59.93, 54.62) * mm, "end": v(58.51, 53.2) * mm});
            skLineSegment(sketch, "E16.1.57.0", {"start": v(48.49, 65) * mm, "end": v(54.28, 60.23) * mm});
            skLineSegment(sketch, "E16.3.57.0", {"start": v(48.49, 65) * mm, "end": v(47.22, 63.45) * mm});
            skLineSegment(sketch, "E16.6.57.0", {"start": v(47.22, 63.45) * mm, "end": v(47.28, 63.4) * mm});
            skArc(sketch, "E16.9.57.0", {"start": v(47.46, 62.47) * mm, "mid": v(47.54, 62.97) * mm, "end": v(47.28, 63.4) * mm});
            skArc(sketch, "E16.13.57.0", {"start": v(47.46, 62.47) * mm, "mid": v(47.12, 61.09) * mm, "end": v(47.45, 59.7) * mm});
            skLineSegment(sketch, "E16.17.57.0", {"start": v(47.45, 59.7) * mm, "end": v(49.3, 58.18) * mm});
            skArc(sketch, "E16.20.57.0", {"start": v(49.3, 58.18) * mm, "mid": v(50.72, 58.13) * mm, "end": v(52, 58.74) * mm});
            skArc(sketch, "E16.24.57.0", {"start": v(52.96, 58.74) * mm, "mid": v(52.48, 58.9) * mm, "end": v(52, 58.74) * mm});
            skLineSegment(sketch, "E16.28.57.0", {"start": v(52.96, 58.74) * mm, "end": v(53.02, 58.69) * mm});
            skLineSegment(sketch, "E16.31.57.0", {"start": v(54.28, 60.23) * mm, "end": v(53.02, 58.69) * mm});
            skLineSegment(sketch, "E16.1.58.0", {"start": v(41.88, 69.43) * mm, "end": v(48.12, 65.27) * mm});
            skLineSegment(sketch, "E16.3.58.0", {"start": v(41.88, 69.43) * mm, "end": v(40.77, 67.77) * mm});
            skLineSegment(sketch, "E16.6.58.0", {"start": v(40.77, 67.77) * mm, "end": v(40.84, 67.73) * mm});
            skArc(sketch, "E16.9.58.0", {"start": v(41.11, 66.82) * mm, "mid": v(41.14, 67.32) * mm, "end": v(40.84, 67.73) * mm});
            skArc(sketch, "E16.13.58.0", {"start": v(41.11, 66.82) * mm, "mid": v(40.9, 65.41) * mm, "end": v(41.37, 64.07) * mm});
            skLineSegment(sketch, "E16.17.58.0", {"start": v(41.37, 64.07) * mm, "end": v(43.36, 62.73) * mm});
            skArc(sketch, "E16.20.58.0", {"start": v(43.36, 62.73) * mm, "mid": v(44.78, 62.82) * mm, "end": v(46, 63.55) * mm});
            skArc(sketch, "E16.24.58.0", {"start": v(46.95, 63.64) * mm, "mid": v(46.46, 63.77) * mm, "end": v(46, 63.55) * mm});
            skLineSegment(sketch, "E16.28.58.0", {"start": v(46.95, 63.64) * mm, "end": v(47, 63.6) * mm});
            skLineSegment(sketch, "E16.31.58.0", {"start": v(48.12, 65.27) * mm, "end": v(47, 63.6) * mm});
            skLineSegment(sketch, "E16.1.59.0", {"start": v(34.88, 73.2) * mm, "end": v(41.5, 69.67) * mm});
            skLineSegment(sketch, "E16.3.59.0", {"start": v(34.88, 73.2) * mm, "end": v(33.93, 71.44) * mm});
            skLineSegment(sketch, "E16.6.59.0", {"start": v(33.93, 71.44) * mm, "end": v(34, 71.4) * mm});
            skArc(sketch, "E16.9.59.0", {"start": v(34.37, 70.53) * mm, "mid": v(34.34, 71.03) * mm, "end": v(34, 71.4) * mm});
            skArc(sketch, "E16.13.59.0", {"start": v(34.37, 70.53) * mm, "mid": v(34.3, 69.1) * mm, "end": v(34.89, 67.81) * mm});
            skLineSegment(sketch, "E16.17.59.0", {"start": v(34.89, 67.81) * mm, "end": v(37, 66.68) * mm});
            skArc(sketch, "E16.20.59.0", {"start": v(37, 66.68) * mm, "mid": v(38.4, 66.9) * mm, "end": v(39.55, 67.76) * mm});
            skArc(sketch, "E16.24.59.0", {"start": v(40.48, 67.94) * mm, "mid": v(39.98, 68.01) * mm, "end": v(39.55, 67.76) * mm});
            skLineSegment(sketch, "E16.28.59.0", {"start": v(40.48, 67.94) * mm, "end": v(40.55, 67.9) * mm});
            skLineSegment(sketch, "E16.31.59.0", {"start": v(41.5, 69.67) * mm, "end": v(40.55, 67.9) * mm});
            skLineSegment(sketch, "E16.1.60.0", {"start": v(27.53, 76.27) * mm, "end": v(34.46, 73.4) * mm});
            skLineSegment(sketch, "E16.3.60.0", {"start": v(27.53, 76.27) * mm, "end": v(26.77, 74.42) * mm});
            skLineSegment(sketch, "E16.6.60.0", {"start": v(26.77, 74.42) * mm, "end": v(26.84, 74.4) * mm});
            skArc(sketch, "E16.9.60.0", {"start": v(27.29, 73.56) * mm, "mid": v(27.21, 74.05) * mm, "end": v(26.84, 74.4) * mm});
            skArc(sketch, "E16.13.60.0", {"start": v(27.29, 73.56) * mm, "mid": v(27.36, 72.13) * mm, "end": v(28.07, 70.9) * mm});
            skLineSegment(sketch, "E16.17.60.0", {"start": v(28.07, 70.9) * mm, "end": v(30.29, 69.99) * mm});
            skArc(sketch, "E16.20.60.0", {"start": v(30.29, 69.99) * mm, "mid": v(31.66, 70.35) * mm, "end": v(32.72, 71.3) * mm});
            skArc(sketch, "E16.24.60.0", {"start": v(33.63, 71.58) * mm, "mid": v(33.12, 71.6) * mm, "end": v(32.72, 71.3) * mm});
            skLineSegment(sketch, "E16.28.60.0", {"start": v(33.63, 71.58) * mm, "end": v(33.7, 71.55) * mm});
            skLineSegment(sketch, "E16.31.60.0", {"start": v(34.46, 73.4) * mm, "end": v(33.7, 71.55) * mm});
            skLineSegment(sketch, "E16.1.61.0", {"start": v(19.92, 78.6) * mm, "end": v(27.1, 76.42) * mm});
            skLineSegment(sketch, "E16.3.61.0", {"start": v(19.92, 78.6) * mm, "end": v(19.34, 76.69) * mm});
            skLineSegment(sketch, "E16.6.61.0", {"start": v(19.34, 76.69) * mm, "end": v(19.42, 76.66) * mm});
            skArc(sketch, "E16.9.61.0", {"start": v(19.95, 75.88) * mm, "mid": v(19.82, 76.37) * mm, "end": v(19.42, 76.66) * mm});
            skArc(sketch, "E16.13.61.0", {"start": v(19.95, 75.88) * mm, "mid": v(20.15, 74.47) * mm, "end": v(20.99, 73.31) * mm});
            skLineSegment(sketch, "E16.17.61.0", {"start": v(20.99, 73.31) * mm, "end": v(23.28, 72.62) * mm});
            skArc(sketch, "E16.20.61.0", {"start": v(23.28, 72.62) * mm, "mid": v(24.62, 73.12) * mm, "end": v(25.57, 74.17) * mm});
            skArc(sketch, "E16.24.61.0", {"start": v(26.45, 74.53) * mm, "mid": v(25.95, 74.5) * mm, "end": v(25.57, 74.17) * mm});
            skLineSegment(sketch, "E16.28.61.0", {"start": v(26.45, 74.53) * mm, "end": v(26.52, 74.5) * mm});
            skLineSegment(sketch, "E16.31.61.0", {"start": v(27.1, 76.42) * mm, "end": v(26.52, 74.5) * mm});
            skLineSegment(sketch, "E16.1.62.0", {"start": v(12.12, 80.18) * mm, "end": v(19.48, 78.71) * mm});
            skLineSegment(sketch, "E16.3.62.0", {"start": v(12.12, 80.18) * mm, "end": v(11.73, 78.21) * mm});
            skLineSegment(sketch, "E16.6.62.0", {"start": v(11.73, 78.21) * mm, "end": v(11.8, 78.2) * mm});
            skArc(sketch, "E16.9.62.0", {"start": v(12.41, 77.47) * mm, "mid": v(12.24, 77.94) * mm, "end": v(11.8, 78.2) * mm});
            skArc(sketch, "E16.13.62.0", {"start": v(12.41, 77.47) * mm, "mid": v(12.76, 76.09) * mm, "end": v(13.7, 75.02) * mm});
            skLineSegment(sketch, "E16.17.62.0", {"start": v(13.7, 75.02) * mm, "end": v(16.05, 74.55) * mm});
            skArc(sketch, "E16.20.62.0", {"start": v(16.05, 74.55) * mm, "mid": v(17.33, 75.18) * mm, "end": v(18.18, 76.32) * mm});
            skArc(sketch, "E16.24.62.0", {"start": v(19.02, 76.77) * mm, "mid": v(18.52, 76.7) * mm, "end": v(18.18, 76.32) * mm});
            skLineSegment(sketch, "E16.28.62.0", {"start": v(19.02, 76.77) * mm, "end": v(19.1, 76.75) * mm});
            skLineSegment(sketch, "E16.31.62.0", {"start": v(19.48, 78.71) * mm, "end": v(19.1, 76.75) * mm});
            skLineSegment(sketch, "E16.1.63.0", {"start": v(4.2, 80.98) * mm, "end": v(11.67, 80.24) * mm});
            skLineSegment(sketch, "E16.3.63.0", {"start": v(4.2, 80.98) * mm, "end": v(4.01, 78.99) * mm});
            skLineSegment(sketch, "E16.6.63.0", {"start": v(4.01, 78.99) * mm, "end": v(4.09, 78.98) * mm});
            skArc(sketch, "E16.9.63.0", {"start": v(4.76, 78.31) * mm, "mid": v(4.54, 78.76) * mm, "end": v(4.09, 78.98) * mm});
            skArc(sketch, "E16.13.63.0", {"start": v(4.76, 78.31) * mm, "mid": v(5.24, 76.97) * mm, "end": v(6.28, 76) * mm});
            skLineSegment(sketch, "E16.17.63.0", {"start": v(6.28, 76) * mm, "end": v(8.67, 75.77) * mm});
            skArc(sketch, "E16.20.63.0", {"start": v(8.67, 75.77) * mm, "mid": v(9.88, 76.51) * mm, "end": v(10.6, 77.73) * mm});
            skArc(sketch, "E16.24.63.0", {"start": v(11.4, 78.26) * mm, "mid": v(10.91, 78.14) * mm, "end": v(10.6, 77.73) * mm});
            skLineSegment(sketch, "E16.28.63.0", {"start": v(11.4, 78.26) * mm, "end": v(11.48, 78.25) * mm});
            skLineSegment(sketch, "E16.31.63.0", {"start": v(11.67, 80.24) * mm, "end": v(11.48, 78.25) * mm});
            skSolve(sketch);
        }
        {
            var Q0;
            Q0=qSketchRegion(id+"F3",true);
            extrude(context, id + "F4", {"entities" : qUnion([Q0]), "operationType" : NewBodyOperationType.REMOVE, "endBound" : BoundingType.THROUGH_ALL, "oppositeDirection" : true, "depth" : 25.4 * mm});
        }
        {
            var Q0;
            Q0=qCreatedBy(makeId("Right.planeOp"),FACE);
            var sketch = newSketch(context, id + "F5", { "sketchPlane" : qUnion([Q0])});
            skLineSegment(sketch, "E17.bottom", {"start": v(0, 80.61) * mm, "end": v(1.5, 80.61) * mm});
            skLineSegment(sketch, "E17.top", {"start": v(0, 75.61) * mm, "end": v(1.5, 75.61) * mm});
            skLineSegment(sketch, "E17.left", {"start": v(0, 80.61) * mm, "end": v(0, 75.61) * mm});
            skLineSegment(sketch, "E17.right", {"start": v(1.5, 80.61) * mm, "end": v(1.5, 75.61) * mm});
            skLineSegment(sketch, "E18", {"start": v(1.5, 80.61) * mm, "end": v(0.86, 83.01) * mm});
            skLineSegment(sketch, "E19", {"start": v(0.86, 83.01) * mm, "end": v(-0.6, 82.62) * mm});
            skLineSegment(sketch, "E20", {"start": v(-0.6, 82.62) * mm, "end": v(0.05, 80.22) * mm});
            skLineSegment(sketch, "E21", {"start": v(0.05, 80.22) * mm, "end": v(1.5, 80.61) * mm});
            skLineSegment(sketch, "E22", {"start": v(15, 102.47) * mm, "end": v(15, -10.74) * mm, "construction": true});
            skLineSegment(sketch, "E23.MirrorCS", {"start": v(29.14, 83.01) * mm, "end": v(30.6, 82.62) * mm});
            skLineSegment(sketch, "E24.MirrorCS", {"start": v(28.5, 80.61) * mm, "end": v(29.14, 83.01) * mm});
            skLineSegment(sketch, "E25.MirrorCS", {"start": v(30.6, 82.62) * mm, "end": v(29.95, 80.22) * mm});
            skLineSegment(sketch, "E26.MirrorCS", {"start": v(28.5, 80.61) * mm, "end": v(28.5, 75.61) * mm});
            skLineSegment(sketch, "E27.MirrorCS", {"start": v(30, 75.61) * mm, "end": v(28.5, 75.61) * mm});
            skLineSegment(sketch, "E28.MirrorCS", {"start": v(30, 80.61) * mm, "end": v(30, 75.61) * mm});
            skLineSegment(sketch, "E29.MirrorCS", {"start": v(29.95, 80.22) * mm, "end": v(28.5, 80.61) * mm});
            skLineSegment(sketch, "E30.MirrorCS", {"start": v(30, 80.61) * mm, "end": v(28.5, 80.61) * mm});
            skSolve(sketch);
        }
        {
            var Q0;
            Q0=qSketchRegion(id+"F5",true);
            var Q1;
            Q1=sQuery(id+"F2.wireOp",EDGE,"E7");
            revolve(context, id + "F6", {"operationType" : NewBodyOperationType.ADD, "entities" : qUnion([Q0]), "axis" : qUnion([Q1]), "revolveType" : RevolveType.FULL});
        }
    });
